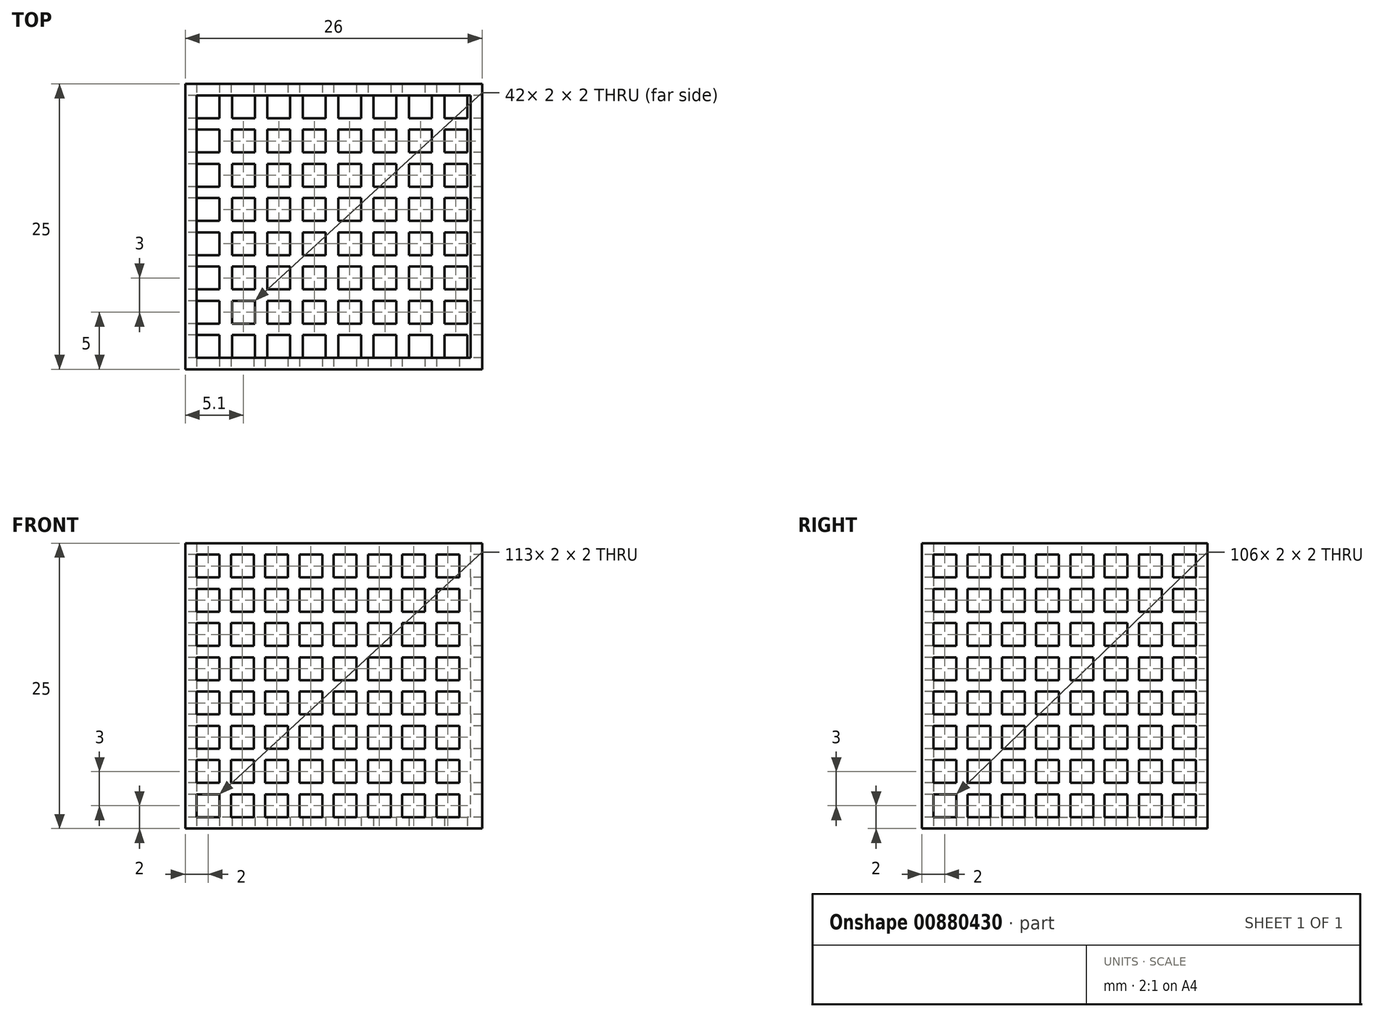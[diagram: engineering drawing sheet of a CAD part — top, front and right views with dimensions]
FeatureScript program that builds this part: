
annotation { "Feature Type Name" : "Feature", "Feature Type Description" : "" }
export const myFeature = defineFeature(function(context is Context, id is Id, definition is map)
    precondition{}
    {
        {
            var Q0;
            Q0=qCreatedBy(makeId("Top.planeOp"),FACE);
            var sketch = newSketch(context, id + "F0", { "sketchPlane" : qUnion([Q0])});
            skLineSegment(sketch, "E0.bottom", {"start": v(13, -12.5) * mm, "end": v(-13, -12.5) * mm});
            skLineSegment(sketch, "E0.top", {"start": v(13, 12.5) * mm, "end": v(-13, 12.5) * mm});
            skLineSegment(sketch, "E0.left", {"start": v(13, -12.5) * mm, "end": v(13, 12.5) * mm});
            skLineSegment(sketch, "E0.right", {"start": v(-13, -12.5) * mm, "end": v(-13, 12.5) * mm});
            skPoint(sketch, "E0.middle", {"position": v(0, 0) * mm});
            skLineSegment(sketch, "E1.bottom", {"start": v(-12, 11.5) * mm, "end": v(-10, 11.5) * mm});
            skLineSegment(sketch, "E1.top", {"start": v(-12, 9.5) * mm, "end": v(-10, 9.5) * mm});
            skLineSegment(sketch, "E1.left", {"start": v(-12, 11.5) * mm, "end": v(-12, 9.5) * mm});
            skLineSegment(sketch, "E1.right", {"start": v(-10, 11.5) * mm, "end": v(-10, 9.5) * mm});
            skLineSegment(sketch, "E2.0.1.0", {"start": v(-12, 8.5) * mm, "end": v(-10, 8.5) * mm});
            skLineSegment(sketch, "E2.0.1.1", {"start": v(-10, 8.5) * mm, "end": v(-10, 6.5) * mm});
            skLineSegment(sketch, "E2.0.1.2", {"start": v(-12, 8.5) * mm, "end": v(-12, 6.5) * mm});
            skLineSegment(sketch, "E2.0.1.3", {"start": v(-12, 6.5) * mm, "end": v(-10, 6.5) * mm});
            skLineSegment(sketch, "E2.0.2.0", {"start": v(-12, 5.5) * mm, "end": v(-10, 5.5) * mm});
            skLineSegment(sketch, "E2.0.2.1", {"start": v(-10, 5.5) * mm, "end": v(-10, 3.5) * mm});
            skLineSegment(sketch, "E2.0.2.2", {"start": v(-12, 5.5) * mm, "end": v(-12, 3.5) * mm});
            skLineSegment(sketch, "E2.0.2.3", {"start": v(-12, 3.5) * mm, "end": v(-10, 3.5) * mm});
            skLineSegment(sketch, "E2.0.3.0", {"start": v(-12, 2.5) * mm, "end": v(-10, 2.5) * mm});
            skLineSegment(sketch, "E2.0.3.1", {"start": v(-10, 2.5) * mm, "end": v(-10, 0.5) * mm});
            skLineSegment(sketch, "E2.0.3.2", {"start": v(-12, 2.5) * mm, "end": v(-12, 0.5) * mm});
            skLineSegment(sketch, "E2.0.3.3", {"start": v(-12, 0.5) * mm, "end": v(-10, 0.5) * mm});
            skLineSegment(sketch, "E2.0.4.0", {"start": v(-12, -0.5) * mm, "end": v(-10, -0.5) * mm});
            skLineSegment(sketch, "E2.0.4.1", {"start": v(-10, -0.5) * mm, "end": v(-10, -2.5) * mm});
            skLineSegment(sketch, "E2.0.4.2", {"start": v(-12, -0.5) * mm, "end": v(-12, -2.5) * mm});
            skLineSegment(sketch, "E2.0.4.3", {"start": v(-12, -2.5) * mm, "end": v(-10, -2.5) * mm});
            skLineSegment(sketch, "E2.0.5.0", {"start": v(-12, -3.5) * mm, "end": v(-10, -3.5) * mm});
            skLineSegment(sketch, "E2.0.5.1", {"start": v(-10, -3.5) * mm, "end": v(-10, -5.5) * mm});
            skLineSegment(sketch, "E2.0.5.2", {"start": v(-12, -3.5) * mm, "end": v(-12, -5.5) * mm});
            skLineSegment(sketch, "E2.0.5.3", {"start": v(-12, -5.5) * mm, "end": v(-10, -5.5) * mm});
            skLineSegment(sketch, "E2.0.6.0", {"start": v(-12, -6.5) * mm, "end": v(-10, -6.5) * mm});
            skLineSegment(sketch, "E2.0.6.1", {"start": v(-10, -6.5) * mm, "end": v(-10, -8.5) * mm});
            skLineSegment(sketch, "E2.0.6.2", {"start": v(-12, -6.5) * mm, "end": v(-12, -8.5) * mm});
            skLineSegment(sketch, "E2.0.6.3", {"start": v(-12, -8.5) * mm, "end": v(-10, -8.5) * mm});
            skLineSegment(sketch, "E2.0.7.0", {"start": v(-12, -9.5) * mm, "end": v(-10, -9.5) * mm});
            skLineSegment(sketch, "E2.0.7.1", {"start": v(-10, -9.5) * mm, "end": v(-10, -11.5) * mm});
            skLineSegment(sketch, "E2.0.7.2", {"start": v(-12, -9.5) * mm, "end": v(-12, -11.5) * mm});
            skLineSegment(sketch, "E2.0.7.3", {"start": v(-12, -11.5) * mm, "end": v(-10, -11.5) * mm});
            skLineSegment(sketch, "E2.1.0.0", {"start": v(-8.9, 11.5) * mm, "end": v(-6.9, 11.5) * mm});
            skLineSegment(sketch, "E2.1.0.1", {"start": v(-6.9, 11.5) * mm, "end": v(-6.9, 9.5) * mm});
            skLineSegment(sketch, "E2.1.0.2", {"start": v(-8.9, 11.5) * mm, "end": v(-8.9, 9.5) * mm});
            skLineSegment(sketch, "E2.1.0.3", {"start": v(-8.9, 9.5) * mm, "end": v(-6.9, 9.5) * mm});
            skLineSegment(sketch, "E2.1.1.0", {"start": v(-8.9, 8.5) * mm, "end": v(-6.9, 8.5) * mm});
            skLineSegment(sketch, "E2.1.1.1", {"start": v(-6.9, 8.5) * mm, "end": v(-6.9, 6.5) * mm});
            skLineSegment(sketch, "E2.1.1.2", {"start": v(-8.9, 8.5) * mm, "end": v(-8.9, 6.5) * mm});
            skLineSegment(sketch, "E2.1.1.3", {"start": v(-8.9, 6.5) * mm, "end": v(-6.9, 6.5) * mm});
            skLineSegment(sketch, "E2.1.2.0", {"start": v(-8.9, 5.5) * mm, "end": v(-6.9, 5.5) * mm});
            skLineSegment(sketch, "E2.1.2.1", {"start": v(-6.9, 5.5) * mm, "end": v(-6.9, 3.5) * mm});
            skLineSegment(sketch, "E2.1.2.2", {"start": v(-8.9, 5.5) * mm, "end": v(-8.9, 3.5) * mm});
            skLineSegment(sketch, "E2.1.2.3", {"start": v(-8.9, 3.5) * mm, "end": v(-6.9, 3.5) * mm});
            skLineSegment(sketch, "E2.1.3.0", {"start": v(-8.9, 2.5) * mm, "end": v(-6.9, 2.5) * mm});
            skLineSegment(sketch, "E2.1.3.1", {"start": v(-6.9, 2.5) * mm, "end": v(-6.9, 0.5) * mm});
            skLineSegment(sketch, "E2.1.3.2", {"start": v(-8.9, 2.5) * mm, "end": v(-8.9, 0.5) * mm});
            skLineSegment(sketch, "E2.1.3.3", {"start": v(-8.9, 0.5) * mm, "end": v(-6.9, 0.5) * mm});
            skLineSegment(sketch, "E2.1.4.0", {"start": v(-8.9, -0.5) * mm, "end": v(-6.9, -0.5) * mm});
            skLineSegment(sketch, "E2.1.4.1", {"start": v(-6.9, -0.5) * mm, "end": v(-6.9, -2.5) * mm});
            skLineSegment(sketch, "E2.1.4.2", {"start": v(-8.9, -0.5) * mm, "end": v(-8.9, -2.5) * mm});
            skLineSegment(sketch, "E2.1.4.3", {"start": v(-8.9, -2.5) * mm, "end": v(-6.9, -2.5) * mm});
            skLineSegment(sketch, "E2.1.5.0", {"start": v(-8.9, -3.5) * mm, "end": v(-6.9, -3.5) * mm});
            skLineSegment(sketch, "E2.1.5.1", {"start": v(-6.9, -3.5) * mm, "end": v(-6.9, -5.5) * mm});
            skLineSegment(sketch, "E2.1.5.2", {"start": v(-8.9, -3.5) * mm, "end": v(-8.9, -5.5) * mm});
            skLineSegment(sketch, "E2.1.5.3", {"start": v(-8.9, -5.5) * mm, "end": v(-6.9, -5.5) * mm});
            skLineSegment(sketch, "E2.1.6.0", {"start": v(-8.9, -6.5) * mm, "end": v(-6.9, -6.5) * mm});
            skLineSegment(sketch, "E2.1.6.1", {"start": v(-6.9, -6.5) * mm, "end": v(-6.9, -8.5) * mm});
            skLineSegment(sketch, "E2.1.6.2", {"start": v(-8.9, -6.5) * mm, "end": v(-8.9, -8.5) * mm});
            skLineSegment(sketch, "E2.1.6.3", {"start": v(-8.9, -8.5) * mm, "end": v(-6.9, -8.5) * mm});
            skLineSegment(sketch, "E2.1.7.0", {"start": v(-8.9, -9.5) * mm, "end": v(-6.9, -9.5) * mm});
            skLineSegment(sketch, "E2.1.7.1", {"start": v(-6.9, -9.5) * mm, "end": v(-6.9, -11.5) * mm});
            skLineSegment(sketch, "E2.1.7.2", {"start": v(-8.9, -9.5) * mm, "end": v(-8.9, -11.5) * mm});
            skLineSegment(sketch, "E2.1.7.3", {"start": v(-8.9, -11.5) * mm, "end": v(-6.9, -11.5) * mm});
            skLineSegment(sketch, "E2.2.0.0", {"start": v(-5.8, 11.5) * mm, "end": v(-3.8, 11.5) * mm});
            skLineSegment(sketch, "E2.2.0.1", {"start": v(-3.8, 11.5) * mm, "end": v(-3.8, 9.5) * mm});
            skLineSegment(sketch, "E2.2.0.2", {"start": v(-5.8, 11.5) * mm, "end": v(-5.8, 9.5) * mm});
            skLineSegment(sketch, "E2.2.0.3", {"start": v(-5.8, 9.5) * mm, "end": v(-3.8, 9.5) * mm});
            skLineSegment(sketch, "E2.2.1.0", {"start": v(-5.8, 8.5) * mm, "end": v(-3.8, 8.5) * mm});
            skLineSegment(sketch, "E2.2.1.1", {"start": v(-3.8, 8.5) * mm, "end": v(-3.8, 6.5) * mm});
            skLineSegment(sketch, "E2.2.1.2", {"start": v(-5.8, 8.5) * mm, "end": v(-5.8, 6.5) * mm});
            skLineSegment(sketch, "E2.2.1.3", {"start": v(-5.8, 6.5) * mm, "end": v(-3.8, 6.5) * mm});
            skLineSegment(sketch, "E2.2.2.0", {"start": v(-5.8, 5.5) * mm, "end": v(-3.8, 5.5) * mm});
            skLineSegment(sketch, "E2.2.2.1", {"start": v(-3.8, 5.5) * mm, "end": v(-3.8, 3.5) * mm});
            skLineSegment(sketch, "E2.2.2.2", {"start": v(-5.8, 5.5) * mm, "end": v(-5.8, 3.5) * mm});
            skLineSegment(sketch, "E2.2.2.3", {"start": v(-5.8, 3.5) * mm, "end": v(-3.8, 3.5) * mm});
            skLineSegment(sketch, "E2.2.3.0", {"start": v(-5.8, 2.5) * mm, "end": v(-3.8, 2.5) * mm});
            skLineSegment(sketch, "E2.2.3.1", {"start": v(-3.8, 2.5) * mm, "end": v(-3.8, 0.5) * mm});
            skLineSegment(sketch, "E2.2.3.2", {"start": v(-5.8, 2.5) * mm, "end": v(-5.8, 0.5) * mm});
            skLineSegment(sketch, "E2.2.3.3", {"start": v(-5.8, 0.5) * mm, "end": v(-3.8, 0.5) * mm});
            skLineSegment(sketch, "E2.2.4.0", {"start": v(-5.8, -0.5) * mm, "end": v(-3.8, -0.5) * mm});
            skLineSegment(sketch, "E2.2.4.1", {"start": v(-3.8, -0.5) * mm, "end": v(-3.8, -2.5) * mm});
            skLineSegment(sketch, "E2.2.4.2", {"start": v(-5.8, -0.5) * mm, "end": v(-5.8, -2.5) * mm});
            skLineSegment(sketch, "E2.2.4.3", {"start": v(-5.8, -2.5) * mm, "end": v(-3.8, -2.5) * mm});
            skLineSegment(sketch, "E2.2.5.0", {"start": v(-5.8, -3.5) * mm, "end": v(-3.8, -3.5) * mm});
            skLineSegment(sketch, "E2.2.5.1", {"start": v(-3.8, -3.5) * mm, "end": v(-3.8, -5.5) * mm});
            skLineSegment(sketch, "E2.2.5.2", {"start": v(-5.8, -3.5) * mm, "end": v(-5.8, -5.5) * mm});
            skLineSegment(sketch, "E2.2.5.3", {"start": v(-5.8, -5.5) * mm, "end": v(-3.8, -5.5) * mm});
            skLineSegment(sketch, "E2.2.6.0", {"start": v(-5.8, -6.5) * mm, "end": v(-3.8, -6.5) * mm});
            skLineSegment(sketch, "E2.2.6.1", {"start": v(-3.8, -6.5) * mm, "end": v(-3.8, -8.5) * mm});
            skLineSegment(sketch, "E2.2.6.2", {"start": v(-5.8, -6.5) * mm, "end": v(-5.8, -8.5) * mm});
            skLineSegment(sketch, "E2.2.6.3", {"start": v(-5.8, -8.5) * mm, "end": v(-3.8, -8.5) * mm});
            skLineSegment(sketch, "E2.2.7.0", {"start": v(-5.8, -9.5) * mm, "end": v(-3.8, -9.5) * mm});
            skLineSegment(sketch, "E2.2.7.1", {"start": v(-3.8, -9.5) * mm, "end": v(-3.8, -11.5) * mm});
            skLineSegment(sketch, "E2.2.7.2", {"start": v(-5.8, -9.5) * mm, "end": v(-5.8, -11.5) * mm});
            skLineSegment(sketch, "E2.2.7.3", {"start": v(-5.8, -11.5) * mm, "end": v(-3.8, -11.5) * mm});
            skLineSegment(sketch, "E2.3.0.0", {"start": v(-2.7, 11.5) * mm, "end": v(-0.7, 11.5) * mm});
            skLineSegment(sketch, "E2.3.0.1", {"start": v(-0.7, 11.5) * mm, "end": v(-0.7, 9.5) * mm});
            skLineSegment(sketch, "E2.3.0.2", {"start": v(-2.7, 11.5) * mm, "end": v(-2.7, 9.5) * mm});
            skLineSegment(sketch, "E2.3.0.3", {"start": v(-2.7, 9.5) * mm, "end": v(-0.7, 9.5) * mm});
            skLineSegment(sketch, "E2.3.1.0", {"start": v(-2.7, 8.5) * mm, "end": v(-0.7, 8.5) * mm});
            skLineSegment(sketch, "E2.3.1.1", {"start": v(-0.7, 8.5) * mm, "end": v(-0.7, 6.5) * mm});
            skLineSegment(sketch, "E2.3.1.2", {"start": v(-2.7, 8.5) * mm, "end": v(-2.7, 6.5) * mm});
            skLineSegment(sketch, "E2.3.1.3", {"start": v(-2.7, 6.5) * mm, "end": v(-0.7, 6.5) * mm});
            skLineSegment(sketch, "E2.3.2.0", {"start": v(-2.7, 5.5) * mm, "end": v(-0.7, 5.5) * mm});
            skLineSegment(sketch, "E2.3.2.1", {"start": v(-0.7, 5.5) * mm, "end": v(-0.7, 3.5) * mm});
            skLineSegment(sketch, "E2.3.2.2", {"start": v(-2.7, 5.5) * mm, "end": v(-2.7, 3.5) * mm});
            skLineSegment(sketch, "E2.3.2.3", {"start": v(-2.7, 3.5) * mm, "end": v(-0.7, 3.5) * mm});
            skLineSegment(sketch, "E2.3.3.0", {"start": v(-2.7, 2.5) * mm, "end": v(-0.7, 2.5) * mm});
            skLineSegment(sketch, "E2.3.3.1", {"start": v(-0.7, 2.5) * mm, "end": v(-0.7, 0.5) * mm});
            skLineSegment(sketch, "E2.3.3.2", {"start": v(-2.7, 2.5) * mm, "end": v(-2.7, 0.5) * mm});
            skLineSegment(sketch, "E2.3.3.3", {"start": v(-2.7, 0.5) * mm, "end": v(-0.7, 0.5) * mm});
            skLineSegment(sketch, "E2.3.4.0", {"start": v(-2.7, -0.5) * mm, "end": v(-0.7, -0.5) * mm});
            skLineSegment(sketch, "E2.3.4.1", {"start": v(-0.7, -0.5) * mm, "end": v(-0.7, -2.5) * mm});
            skLineSegment(sketch, "E2.3.4.2", {"start": v(-2.7, -0.5) * mm, "end": v(-2.7, -2.5) * mm});
            skLineSegment(sketch, "E2.3.4.3", {"start": v(-2.7, -2.5) * mm, "end": v(-0.7, -2.5) * mm});
            skLineSegment(sketch, "E2.3.5.0", {"start": v(-2.7, -3.5) * mm, "end": v(-0.7, -3.5) * mm});
            skLineSegment(sketch, "E2.3.5.1", {"start": v(-0.7, -3.5) * mm, "end": v(-0.7, -5.5) * mm});
            skLineSegment(sketch, "E2.3.5.2", {"start": v(-2.7, -3.5) * mm, "end": v(-2.7, -5.5) * mm});
            skLineSegment(sketch, "E2.3.5.3", {"start": v(-2.7, -5.5) * mm, "end": v(-0.7, -5.5) * mm});
            skLineSegment(sketch, "E2.3.6.0", {"start": v(-2.7, -6.5) * mm, "end": v(-0.7, -6.5) * mm});
            skLineSegment(sketch, "E2.3.6.1", {"start": v(-0.7, -6.5) * mm, "end": v(-0.7, -8.5) * mm});
            skLineSegment(sketch, "E2.3.6.2", {"start": v(-2.7, -6.5) * mm, "end": v(-2.7, -8.5) * mm});
            skLineSegment(sketch, "E2.3.6.3", {"start": v(-2.7, -8.5) * mm, "end": v(-0.7, -8.5) * mm});
            skLineSegment(sketch, "E2.3.7.0", {"start": v(-2.7, -9.5) * mm, "end": v(-0.7, -9.5) * mm});
            skLineSegment(sketch, "E2.3.7.1", {"start": v(-0.7, -9.5) * mm, "end": v(-0.7, -11.5) * mm});
            skLineSegment(sketch, "E2.3.7.2", {"start": v(-2.7, -9.5) * mm, "end": v(-2.7, -11.5) * mm});
            skLineSegment(sketch, "E2.3.7.3", {"start": v(-2.7, -11.5) * mm, "end": v(-0.7, -11.5) * mm});
            skLineSegment(sketch, "E2.4.0.0", {"start": v(0.4, 11.5) * mm, "end": v(2.4, 11.5) * mm});
            skLineSegment(sketch, "E2.4.0.1", {"start": v(2.4, 11.5) * mm, "end": v(2.4, 9.5) * mm});
            skLineSegment(sketch, "E2.4.0.2", {"start": v(0.4, 11.5) * mm, "end": v(0.4, 9.5) * mm});
            skLineSegment(sketch, "E2.4.0.3", {"start": v(0.4, 9.5) * mm, "end": v(2.4, 9.5) * mm});
            skLineSegment(sketch, "E2.4.1.0", {"start": v(0.4, 8.5) * mm, "end": v(2.4, 8.5) * mm});
            skLineSegment(sketch, "E2.4.1.1", {"start": v(2.4, 8.5) * mm, "end": v(2.4, 6.5) * mm});
            skLineSegment(sketch, "E2.4.1.2", {"start": v(0.4, 8.5) * mm, "end": v(0.4, 6.5) * mm});
            skLineSegment(sketch, "E2.4.1.3", {"start": v(0.4, 6.5) * mm, "end": v(2.4, 6.5) * mm});
            skLineSegment(sketch, "E2.4.2.0", {"start": v(0.4, 5.5) * mm, "end": v(2.4, 5.5) * mm});
            skLineSegment(sketch, "E2.4.2.1", {"start": v(2.4, 5.5) * mm, "end": v(2.4, 3.5) * mm});
            skLineSegment(sketch, "E2.4.2.2", {"start": v(0.4, 5.5) * mm, "end": v(0.4, 3.5) * mm});
            skLineSegment(sketch, "E2.4.2.3", {"start": v(0.4, 3.5) * mm, "end": v(2.4, 3.5) * mm});
            skLineSegment(sketch, "E2.4.3.0", {"start": v(0.4, 2.5) * mm, "end": v(2.4, 2.5) * mm});
            skLineSegment(sketch, "E2.4.3.1", {"start": v(2.4, 2.5) * mm, "end": v(2.4, 0.5) * mm});
            skLineSegment(sketch, "E2.4.3.2", {"start": v(0.4, 2.5) * mm, "end": v(0.4, 0.5) * mm});
            skLineSegment(sketch, "E2.4.3.3", {"start": v(0.4, 0.5) * mm, "end": v(2.4, 0.5) * mm});
            skLineSegment(sketch, "E2.4.4.0", {"start": v(0.4, -0.5) * mm, "end": v(2.4, -0.5) * mm});
            skLineSegment(sketch, "E2.4.4.1", {"start": v(2.4, -0.5) * mm, "end": v(2.4, -2.5) * mm});
            skLineSegment(sketch, "E2.4.4.2", {"start": v(0.4, -0.5) * mm, "end": v(0.4, -2.5) * mm});
            skLineSegment(sketch, "E2.4.4.3", {"start": v(0.4, -2.5) * mm, "end": v(2.4, -2.5) * mm});
            skLineSegment(sketch, "E2.4.5.0", {"start": v(0.4, -3.5) * mm, "end": v(2.4, -3.5) * mm});
            skLineSegment(sketch, "E2.4.5.1", {"start": v(2.4, -3.5) * mm, "end": v(2.4, -5.5) * mm});
            skLineSegment(sketch, "E2.4.5.2", {"start": v(0.4, -3.5) * mm, "end": v(0.4, -5.5) * mm});
            skLineSegment(sketch, "E2.4.5.3", {"start": v(0.4, -5.5) * mm, "end": v(2.4, -5.5) * mm});
            skLineSegment(sketch, "E2.4.6.0", {"start": v(0.4, -6.5) * mm, "end": v(2.4, -6.5) * mm});
            skLineSegment(sketch, "E2.4.6.1", {"start": v(2.4, -6.5) * mm, "end": v(2.4, -8.5) * mm});
            skLineSegment(sketch, "E2.4.6.2", {"start": v(0.4, -6.5) * mm, "end": v(0.4, -8.5) * mm});
            skLineSegment(sketch, "E2.4.6.3", {"start": v(0.4, -8.5) * mm, "end": v(2.4, -8.5) * mm});
            skLineSegment(sketch, "E2.4.7.0", {"start": v(0.4, -9.5) * mm, "end": v(2.4, -9.5) * mm});
            skLineSegment(sketch, "E2.4.7.1", {"start": v(2.4, -9.5) * mm, "end": v(2.4, -11.5) * mm});
            skLineSegment(sketch, "E2.4.7.2", {"start": v(0.4, -9.5) * mm, "end": v(0.4, -11.5) * mm});
            skLineSegment(sketch, "E2.4.7.3", {"start": v(0.4, -11.5) * mm, "end": v(2.4, -11.5) * mm});
            skLineSegment(sketch, "E2.5.0.0", {"start": v(3.5, 11.5) * mm, "end": v(5.5, 11.5) * mm});
            skLineSegment(sketch, "E2.5.0.1", {"start": v(5.5, 11.5) * mm, "end": v(5.5, 9.5) * mm});
            skLineSegment(sketch, "E2.5.0.2", {"start": v(3.5, 11.5) * mm, "end": v(3.5, 9.5) * mm});
            skLineSegment(sketch, "E2.5.0.3", {"start": v(3.5, 9.5) * mm, "end": v(5.5, 9.5) * mm});
            skLineSegment(sketch, "E2.5.1.0", {"start": v(3.5, 8.5) * mm, "end": v(5.5, 8.5) * mm});
            skLineSegment(sketch, "E2.5.1.1", {"start": v(5.5, 8.5) * mm, "end": v(5.5, 6.5) * mm});
            skLineSegment(sketch, "E2.5.1.2", {"start": v(3.5, 8.5) * mm, "end": v(3.5, 6.5) * mm});
            skLineSegment(sketch, "E2.5.1.3", {"start": v(3.5, 6.5) * mm, "end": v(5.5, 6.5) * mm});
            skLineSegment(sketch, "E2.5.2.0", {"start": v(3.5, 5.5) * mm, "end": v(5.5, 5.5) * mm});
            skLineSegment(sketch, "E2.5.2.1", {"start": v(5.5, 5.5) * mm, "end": v(5.5, 3.5) * mm});
            skLineSegment(sketch, "E2.5.2.2", {"start": v(3.5, 5.5) * mm, "end": v(3.5, 3.5) * mm});
            skLineSegment(sketch, "E2.5.2.3", {"start": v(3.5, 3.5) * mm, "end": v(5.5, 3.5) * mm});
            skLineSegment(sketch, "E2.5.3.0", {"start": v(3.5, 2.5) * mm, "end": v(5.5, 2.5) * mm});
            skLineSegment(sketch, "E2.5.3.1", {"start": v(5.5, 2.5) * mm, "end": v(5.5, 0.5) * mm});
            skLineSegment(sketch, "E2.5.3.2", {"start": v(3.5, 2.5) * mm, "end": v(3.5, 0.5) * mm});
            skLineSegment(sketch, "E2.5.3.3", {"start": v(3.5, 0.5) * mm, "end": v(5.5, 0.5) * mm});
            skLineSegment(sketch, "E2.5.4.0", {"start": v(3.5, -0.5) * mm, "end": v(5.5, -0.5) * mm});
            skLineSegment(sketch, "E2.5.4.1", {"start": v(5.5, -0.5) * mm, "end": v(5.5, -2.5) * mm});
            skLineSegment(sketch, "E2.5.4.2", {"start": v(3.5, -0.5) * mm, "end": v(3.5, -2.5) * mm});
            skLineSegment(sketch, "E2.5.4.3", {"start": v(3.5, -2.5) * mm, "end": v(5.5, -2.5) * mm});
            skLineSegment(sketch, "E2.5.5.0", {"start": v(3.5, -3.5) * mm, "end": v(5.5, -3.5) * mm});
            skLineSegment(sketch, "E2.5.5.1", {"start": v(5.5, -3.5) * mm, "end": v(5.5, -5.5) * mm});
            skLineSegment(sketch, "E2.5.5.2", {"start": v(3.5, -3.5) * mm, "end": v(3.5, -5.5) * mm});
            skLineSegment(sketch, "E2.5.5.3", {"start": v(3.5, -5.5) * mm, "end": v(5.5, -5.5) * mm});
            skLineSegment(sketch, "E2.5.6.0", {"start": v(3.5, -6.5) * mm, "end": v(5.5, -6.5) * mm});
            skLineSegment(sketch, "E2.5.6.1", {"start": v(5.5, -6.5) * mm, "end": v(5.5, -8.5) * mm});
            skLineSegment(sketch, "E2.5.6.2", {"start": v(3.5, -6.5) * mm, "end": v(3.5, -8.5) * mm});
            skLineSegment(sketch, "E2.5.6.3", {"start": v(3.5, -8.5) * mm, "end": v(5.5, -8.5) * mm});
            skLineSegment(sketch, "E2.5.7.0", {"start": v(3.5, -9.5) * mm, "end": v(5.5, -9.5) * mm});
            skLineSegment(sketch, "E2.5.7.1", {"start": v(5.5, -9.5) * mm, "end": v(5.5, -11.5) * mm});
            skLineSegment(sketch, "E2.5.7.2", {"start": v(3.5, -9.5) * mm, "end": v(3.5, -11.5) * mm});
            skLineSegment(sketch, "E2.5.7.3", {"start": v(3.5, -11.5) * mm, "end": v(5.5, -11.5) * mm});
            skLineSegment(sketch, "E2.6.0.0", {"start": v(6.6, 11.5) * mm, "end": v(8.6, 11.5) * mm});
            skLineSegment(sketch, "E2.6.0.1", {"start": v(8.6, 11.5) * mm, "end": v(8.6, 9.5) * mm});
            skLineSegment(sketch, "E2.6.0.2", {"start": v(6.6, 11.5) * mm, "end": v(6.6, 9.5) * mm});
            skLineSegment(sketch, "E2.6.0.3", {"start": v(6.6, 9.5) * mm, "end": v(8.6, 9.5) * mm});
            skLineSegment(sketch, "E2.6.1.0", {"start": v(6.6, 8.5) * mm, "end": v(8.6, 8.5) * mm});
            skLineSegment(sketch, "E2.6.1.1", {"start": v(8.6, 8.5) * mm, "end": v(8.6, 6.5) * mm});
            skLineSegment(sketch, "E2.6.1.2", {"start": v(6.6, 8.5) * mm, "end": v(6.6, 6.5) * mm});
            skLineSegment(sketch, "E2.6.1.3", {"start": v(6.6, 6.5) * mm, "end": v(8.6, 6.5) * mm});
            skLineSegment(sketch, "E2.6.2.0", {"start": v(6.6, 5.5) * mm, "end": v(8.6, 5.5) * mm});
            skLineSegment(sketch, "E2.6.2.1", {"start": v(8.6, 5.5) * mm, "end": v(8.6, 3.5) * mm});
            skLineSegment(sketch, "E2.6.2.2", {"start": v(6.6, 5.5) * mm, "end": v(6.6, 3.5) * mm});
            skLineSegment(sketch, "E2.6.2.3", {"start": v(6.6, 3.5) * mm, "end": v(8.6, 3.5) * mm});
            skLineSegment(sketch, "E2.6.3.0", {"start": v(6.6, 2.5) * mm, "end": v(8.6, 2.5) * mm});
            skLineSegment(sketch, "E2.6.3.1", {"start": v(8.6, 2.5) * mm, "end": v(8.6, 0.5) * mm});
            skLineSegment(sketch, "E2.6.3.2", {"start": v(6.6, 2.5) * mm, "end": v(6.6, 0.5) * mm});
            skLineSegment(sketch, "E2.6.3.3", {"start": v(6.6, 0.5) * mm, "end": v(8.6, 0.5) * mm});
            skLineSegment(sketch, "E2.6.4.0", {"start": v(6.6, -0.5) * mm, "end": v(8.6, -0.5) * mm});
            skLineSegment(sketch, "E2.6.4.1", {"start": v(8.6, -0.5) * mm, "end": v(8.6, -2.5) * mm});
            skLineSegment(sketch, "E2.6.4.2", {"start": v(6.6, -0.5) * mm, "end": v(6.6, -2.5) * mm});
            skLineSegment(sketch, "E2.6.4.3", {"start": v(6.6, -2.5) * mm, "end": v(8.6, -2.5) * mm});
            skLineSegment(sketch, "E2.6.5.0", {"start": v(6.6, -3.5) * mm, "end": v(8.6, -3.5) * mm});
            skLineSegment(sketch, "E2.6.5.1", {"start": v(8.6, -3.5) * mm, "end": v(8.6, -5.5) * mm});
            skLineSegment(sketch, "E2.6.5.2", {"start": v(6.6, -3.5) * mm, "end": v(6.6, -5.5) * mm});
            skLineSegment(sketch, "E2.6.5.3", {"start": v(6.6, -5.5) * mm, "end": v(8.6, -5.5) * mm});
            skLineSegment(sketch, "E2.6.6.0", {"start": v(6.6, -6.5) * mm, "end": v(8.6, -6.5) * mm});
            skLineSegment(sketch, "E2.6.6.1", {"start": v(8.6, -6.5) * mm, "end": v(8.6, -8.5) * mm});
            skLineSegment(sketch, "E2.6.6.2", {"start": v(6.6, -6.5) * mm, "end": v(6.6, -8.5) * mm});
            skLineSegment(sketch, "E2.6.6.3", {"start": v(6.6, -8.5) * mm, "end": v(8.6, -8.5) * mm});
            skLineSegment(sketch, "E2.6.7.0", {"start": v(6.6, -9.5) * mm, "end": v(8.6, -9.5) * mm});
            skLineSegment(sketch, "E2.6.7.1", {"start": v(8.6, -9.5) * mm, "end": v(8.6, -11.5) * mm});
            skLineSegment(sketch, "E2.6.7.2", {"start": v(6.6, -9.5) * mm, "end": v(6.6, -11.5) * mm});
            skLineSegment(sketch, "E2.6.7.3", {"start": v(6.6, -11.5) * mm, "end": v(8.6, -11.5) * mm});
            skLineSegment(sketch, "E2.7.0.0", {"start": v(9.7, 11.5) * mm, "end": v(11.7, 11.5) * mm});
            skLineSegment(sketch, "E2.7.0.1", {"start": v(11.7, 11.5) * mm, "end": v(11.7, 9.5) * mm});
            skLineSegment(sketch, "E2.7.0.2", {"start": v(9.7, 11.5) * mm, "end": v(9.7, 9.5) * mm});
            skLineSegment(sketch, "E2.7.0.3", {"start": v(9.7, 9.5) * mm, "end": v(11.7, 9.5) * mm});
            skLineSegment(sketch, "E2.7.1.0", {"start": v(9.7, 8.5) * mm, "end": v(11.7, 8.5) * mm});
            skLineSegment(sketch, "E2.7.1.1", {"start": v(11.7, 8.5) * mm, "end": v(11.7, 6.5) * mm});
            skLineSegment(sketch, "E2.7.1.2", {"start": v(9.7, 8.5) * mm, "end": v(9.7, 6.5) * mm});
            skLineSegment(sketch, "E2.7.1.3", {"start": v(9.7, 6.5) * mm, "end": v(11.7, 6.5) * mm});
            skLineSegment(sketch, "E2.7.2.0", {"start": v(9.7, 5.5) * mm, "end": v(11.7, 5.5) * mm});
            skLineSegment(sketch, "E2.7.2.1", {"start": v(11.7, 5.5) * mm, "end": v(11.7, 3.5) * mm});
            skLineSegment(sketch, "E2.7.2.2", {"start": v(9.7, 5.5) * mm, "end": v(9.7, 3.5) * mm});
            skLineSegment(sketch, "E2.7.2.3", {"start": v(9.7, 3.5) * mm, "end": v(11.7, 3.5) * mm});
            skLineSegment(sketch, "E2.7.3.0", {"start": v(9.7, 2.5) * mm, "end": v(11.7, 2.5) * mm});
            skLineSegment(sketch, "E2.7.3.1", {"start": v(11.7, 2.5) * mm, "end": v(11.7, 0.5) * mm});
            skLineSegment(sketch, "E2.7.3.2", {"start": v(9.7, 2.5) * mm, "end": v(9.7, 0.5) * mm});
            skLineSegment(sketch, "E2.7.3.3", {"start": v(9.7, 0.5) * mm, "end": v(11.7, 0.5) * mm});
            skLineSegment(sketch, "E2.7.4.0", {"start": v(9.7, -0.5) * mm, "end": v(11.7, -0.5) * mm});
            skLineSegment(sketch, "E2.7.4.1", {"start": v(11.7, -0.5) * mm, "end": v(11.7, -2.5) * mm});
            skLineSegment(sketch, "E2.7.4.2", {"start": v(9.7, -0.5) * mm, "end": v(9.7, -2.5) * mm});
            skLineSegment(sketch, "E2.7.4.3", {"start": v(9.7, -2.5) * mm, "end": v(11.7, -2.5) * mm});
            skLineSegment(sketch, "E2.7.5.0", {"start": v(9.7, -3.5) * mm, "end": v(11.7, -3.5) * mm});
            skLineSegment(sketch, "E2.7.5.1", {"start": v(11.7, -3.5) * mm, "end": v(11.7, -5.5) * mm});
            skLineSegment(sketch, "E2.7.5.2", {"start": v(9.7, -3.5) * mm, "end": v(9.7, -5.5) * mm});
            skLineSegment(sketch, "E2.7.5.3", {"start": v(9.7, -5.5) * mm, "end": v(11.7, -5.5) * mm});
            skLineSegment(sketch, "E2.7.6.0", {"start": v(9.7, -6.5) * mm, "end": v(11.7, -6.5) * mm});
            skLineSegment(sketch, "E2.7.6.1", {"start": v(11.7, -6.5) * mm, "end": v(11.7, -8.5) * mm});
            skLineSegment(sketch, "E2.7.6.2", {"start": v(9.7, -6.5) * mm, "end": v(9.7, -8.5) * mm});
            skLineSegment(sketch, "E2.7.6.3", {"start": v(9.7, -8.5) * mm, "end": v(11.7, -8.5) * mm});
            skLineSegment(sketch, "E2.7.7.0", {"start": v(9.7, -9.5) * mm, "end": v(11.7, -9.5) * mm});
            skLineSegment(sketch, "E2.7.7.1", {"start": v(11.7, -9.5) * mm, "end": v(11.7, -11.5) * mm});
            skLineSegment(sketch, "E2.7.7.2", {"start": v(9.7, -9.5) * mm, "end": v(9.7, -11.5) * mm});
            skLineSegment(sketch, "E2.7.7.3", {"start": v(9.7, -11.5) * mm, "end": v(11.7, -11.5) * mm});
            skLineSegment(sketch, "E2.direction1", {"start": v(-12, 9.5) * mm, "end": v(-8.9, 9.5) * mm, "construction": true});
            skLineSegment(sketch, "E2.direction2", {"start": v(-12, 9.5) * mm, "end": v(-12, 6.5) * mm, "construction": true});
            skSolve(sketch);
        }
        {
            var Q0;
            Q0=makeQuery(id+"F0.imprint","IMPRINT",FACE,{"disambiguationData":[TD([[makeQuery(id+"F0.imprint","IMPRINT",EDGE,{"derivedFrom":sQuery(id+"F0.wireOp",EDGE,"E0.bottom")}),-1.0]])]});
            extrude(context, id + "F1", {"entities" : qUnion([Q0]), "depth" : 1 * mm, "offsetDistance" : 25 * mm});
        }
        {
            var Q0;
            Q0=makeQuery(id+"F1.opExtrude","CAP_FACE",FACE,{"disambiguationData":[OSD([sQuery(id+"F0.wireOp",EDGE,"E0.bottom"),sQuery(id+"F0.wireOp",EDGE,"E0.top"),sQuery(id+"F0.wireOp",EDGE,"E0.left"),sQuery(id+"F0.wireOp",EDGE,"E0.right"),sQuery(id+"F0.wireOp",EDGE,"E1.bottom"),sQuery(id+"F0.wireOp",EDGE,"E1.top"),sQuery(id+"F0.wireOp",EDGE,"E1.left"),sQuery(id+"F0.wireOp",EDGE,"E1.right"),sQuery(id+"F0.wireOp",EDGE,"E2.0.1.0"),sQuery(id+"F0.wireOp",EDGE,"E2.0.1.1"),sQuery(id+"F0.wireOp",EDGE,"E2.0.1.2"),sQuery(id+"F0.wireOp",EDGE,"E2.0.1.3"),sQuery(id+"F0.wireOp",EDGE,"E2.0.2.0"),sQuery(id+"F0.wireOp",EDGE,"E2.0.2.1"),sQuery(id+"F0.wireOp",EDGE,"E2.0.2.2"),sQuery(id+"F0.wireOp",EDGE,"E2.0.2.3"),sQuery(id+"F0.wireOp",EDGE,"E2.0.3.0"),sQuery(id+"F0.wireOp",EDGE,"E2.0.3.1"),sQuery(id+"F0.wireOp",EDGE,"E2.0.3.2"),sQuery(id+"F0.wireOp",EDGE,"E2.0.3.3"),sQuery(id+"F0.wireOp",EDGE,"E2.0.4.0"),sQuery(id+"F0.wireOp",EDGE,"E2.0.4.1"),sQuery(id+"F0.wireOp",EDGE,"E2.0.4.2"),sQuery(id+"F0.wireOp",EDGE,"E2.0.4.3"),sQuery(id+"F0.wireOp",EDGE,"E2.0.5.0"),sQuery(id+"F0.wireOp",EDGE,"E2.0.5.1"),sQuery(id+"F0.wireOp",EDGE,"E2.0.5.2"),sQuery(id+"F0.wireOp",EDGE,"E2.0.5.3"),sQuery(id+"F0.wireOp",EDGE,"E2.0.6.0"),sQuery(id+"F0.wireOp",EDGE,"E2.0.6.1"),sQuery(id+"F0.wireOp",EDGE,"E2.0.6.2"),sQuery(id+"F0.wireOp",EDGE,"E2.0.6.3"),sQuery(id+"F0.wireOp",EDGE,"E2.0.7.0"),sQuery(id+"F0.wireOp",EDGE,"E2.0.7.1"),sQuery(id+"F0.wireOp",EDGE,"E2.0.7.2"),sQuery(id+"F0.wireOp",EDGE,"E2.0.7.3"),sQuery(id+"F0.wireOp",EDGE,"E2.1.0.0"),sQuery(id+"F0.wireOp",EDGE,"E2.1.0.1"),sQuery(id+"F0.wireOp",EDGE,"E2.1.0.2"),sQuery(id+"F0.wireOp",EDGE,"E2.1.0.3"),sQuery(id+"F0.wireOp",EDGE,"E2.1.1.0"),sQuery(id+"F0.wireOp",EDGE,"E2.1.1.1"),sQuery(id+"F0.wireOp",EDGE,"E2.1.1.2"),sQuery(id+"F0.wireOp",EDGE,"E2.1.1.3"),sQuery(id+"F0.wireOp",EDGE,"E2.1.2.0"),sQuery(id+"F0.wireOp",EDGE,"E2.1.2.1"),sQuery(id+"F0.wireOp",EDGE,"E2.1.2.2"),sQuery(id+"F0.wireOp",EDGE,"E2.1.2.3"),sQuery(id+"F0.wireOp",EDGE,"E2.1.3.0"),sQuery(id+"F0.wireOp",EDGE,"E2.1.3.1"),sQuery(id+"F0.wireOp",EDGE,"E2.1.3.2"),sQuery(id+"F0.wireOp",EDGE,"E2.1.3.3"),sQuery(id+"F0.wireOp",EDGE,"E2.1.4.0"),sQuery(id+"F0.wireOp",EDGE,"E2.1.4.1"),sQuery(id+"F0.wireOp",EDGE,"E2.1.4.2"),sQuery(id+"F0.wireOp",EDGE,"E2.1.4.3"),sQuery(id+"F0.wireOp",EDGE,"E2.1.5.0"),sQuery(id+"F0.wireOp",EDGE,"E2.1.5.1"),sQuery(id+"F0.wireOp",EDGE,"E2.1.5.2"),sQuery(id+"F0.wireOp",EDGE,"E2.1.5.3"),sQuery(id+"F0.wireOp",EDGE,"E2.1.6.0"),sQuery(id+"F0.wireOp",EDGE,"E2.1.6.1"),sQuery(id+"F0.wireOp",EDGE,"E2.1.6.2"),sQuery(id+"F0.wireOp",EDGE,"E2.1.6.3"),sQuery(id+"F0.wireOp",EDGE,"E2.1.7.0"),sQuery(id+"F0.wireOp",EDGE,"E2.1.7.1"),sQuery(id+"F0.wireOp",EDGE,"E2.1.7.2"),sQuery(id+"F0.wireOp",EDGE,"E2.1.7.3"),sQuery(id+"F0.wireOp",EDGE,"E2.2.0.0"),sQuery(id+"F0.wireOp",EDGE,"E2.2.0.1"),sQuery(id+"F0.wireOp",EDGE,"E2.2.0.2"),sQuery(id+"F0.wireOp",EDGE,"E2.2.0.3"),sQuery(id+"F0.wireOp",EDGE,"E2.2.1.0"),sQuery(id+"F0.wireOp",EDGE,"E2.2.1.1"),sQuery(id+"F0.wireOp",EDGE,"E2.2.1.2"),sQuery(id+"F0.wireOp",EDGE,"E2.2.1.3"),sQuery(id+"F0.wireOp",EDGE,"E2.2.2.0"),sQuery(id+"F0.wireOp",EDGE,"E2.2.2.1"),sQuery(id+"F0.wireOp",EDGE,"E2.2.2.2"),sQuery(id+"F0.wireOp",EDGE,"E2.2.2.3"),sQuery(id+"F0.wireOp",EDGE,"E2.2.3.0"),sQuery(id+"F0.wireOp",EDGE,"E2.2.3.1"),sQuery(id+"F0.wireOp",EDGE,"E2.2.3.2"),sQuery(id+"F0.wireOp",EDGE,"E2.2.3.3"),sQuery(id+"F0.wireOp",EDGE,"E2.2.4.0"),sQuery(id+"F0.wireOp",EDGE,"E2.2.4.1"),sQuery(id+"F0.wireOp",EDGE,"E2.2.4.2"),sQuery(id+"F0.wireOp",EDGE,"E2.2.4.3"),sQuery(id+"F0.wireOp",EDGE,"E2.2.5.0"),sQuery(id+"F0.wireOp",EDGE,"E2.2.5.1"),sQuery(id+"F0.wireOp",EDGE,"E2.2.5.2"),sQuery(id+"F0.wireOp",EDGE,"E2.2.5.3"),sQuery(id+"F0.wireOp",EDGE,"E2.2.6.0"),sQuery(id+"F0.wireOp",EDGE,"E2.2.6.1"),sQuery(id+"F0.wireOp",EDGE,"E2.2.6.2"),sQuery(id+"F0.wireOp",EDGE,"E2.2.6.3"),sQuery(id+"F0.wireOp",EDGE,"E2.2.7.0"),sQuery(id+"F0.wireOp",EDGE,"E2.2.7.1"),sQuery(id+"F0.wireOp",EDGE,"E2.2.7.2"),sQuery(id+"F0.wireOp",EDGE,"E2.2.7.3"),sQuery(id+"F0.wireOp",EDGE,"E2.3.0.0"),sQuery(id+"F0.wireOp",EDGE,"E2.3.0.1"),sQuery(id+"F0.wireOp",EDGE,"E2.3.0.2"),sQuery(id+"F0.wireOp",EDGE,"E2.3.0.3"),sQuery(id+"F0.wireOp",EDGE,"E2.3.1.0"),sQuery(id+"F0.wireOp",EDGE,"E2.3.1.1"),sQuery(id+"F0.wireOp",EDGE,"E2.3.1.2"),sQuery(id+"F0.wireOp",EDGE,"E2.3.1.3"),sQuery(id+"F0.wireOp",EDGE,"E2.3.2.0"),sQuery(id+"F0.wireOp",EDGE,"E2.3.2.1"),sQuery(id+"F0.wireOp",EDGE,"E2.3.2.2"),sQuery(id+"F0.wireOp",EDGE,"E2.3.2.3"),sQuery(id+"F0.wireOp",EDGE,"E2.3.3.0"),sQuery(id+"F0.wireOp",EDGE,"E2.3.3.1"),sQuery(id+"F0.wireOp",EDGE,"E2.3.3.2"),sQuery(id+"F0.wireOp",EDGE,"E2.3.3.3"),sQuery(id+"F0.wireOp",EDGE,"E2.3.4.0"),sQuery(id+"F0.wireOp",EDGE,"E2.3.4.1"),sQuery(id+"F0.wireOp",EDGE,"E2.3.4.2"),sQuery(id+"F0.wireOp",EDGE,"E2.3.4.3"),sQuery(id+"F0.wireOp",EDGE,"E2.3.5.0"),sQuery(id+"F0.wireOp",EDGE,"E2.3.5.1"),sQuery(id+"F0.wireOp",EDGE,"E2.3.5.2"),sQuery(id+"F0.wireOp",EDGE,"E2.3.5.3"),sQuery(id+"F0.wireOp",EDGE,"E2.3.6.0"),sQuery(id+"F0.wireOp",EDGE,"E2.3.6.1"),sQuery(id+"F0.wireOp",EDGE,"E2.3.6.2"),sQuery(id+"F0.wireOp",EDGE,"E2.3.6.3"),sQuery(id+"F0.wireOp",EDGE,"E2.3.7.0"),sQuery(id+"F0.wireOp",EDGE,"E2.3.7.1"),sQuery(id+"F0.wireOp",EDGE,"E2.3.7.2"),sQuery(id+"F0.wireOp",EDGE,"E2.3.7.3"),sQuery(id+"F0.wireOp",EDGE,"E2.4.0.0"),sQuery(id+"F0.wireOp",EDGE,"E2.4.0.1"),sQuery(id+"F0.wireOp",EDGE,"E2.4.0.2"),sQuery(id+"F0.wireOp",EDGE,"E2.4.0.3"),sQuery(id+"F0.wireOp",EDGE,"E2.4.1.0"),sQuery(id+"F0.wireOp",EDGE,"E2.4.1.1"),sQuery(id+"F0.wireOp",EDGE,"E2.4.1.2"),sQuery(id+"F0.wireOp",EDGE,"E2.4.1.3"),sQuery(id+"F0.wireOp",EDGE,"E2.4.2.0"),sQuery(id+"F0.wireOp",EDGE,"E2.4.2.1"),sQuery(id+"F0.wireOp",EDGE,"E2.4.2.2"),sQuery(id+"F0.wireOp",EDGE,"E2.4.2.3"),sQuery(id+"F0.wireOp",EDGE,"E2.4.3.0"),sQuery(id+"F0.wireOp",EDGE,"E2.4.3.1"),sQuery(id+"F0.wireOp",EDGE,"E2.4.3.2"),sQuery(id+"F0.wireOp",EDGE,"E2.4.3.3"),sQuery(id+"F0.wireOp",EDGE,"E2.4.4.0"),sQuery(id+"F0.wireOp",EDGE,"E2.4.4.1"),sQuery(id+"F0.wireOp",EDGE,"E2.4.4.2"),sQuery(id+"F0.wireOp",EDGE,"E2.4.4.3"),sQuery(id+"F0.wireOp",EDGE,"E2.4.5.0"),sQuery(id+"F0.wireOp",EDGE,"E2.4.5.1"),sQuery(id+"F0.wireOp",EDGE,"E2.4.5.2"),sQuery(id+"F0.wireOp",EDGE,"E2.4.5.3"),sQuery(id+"F0.wireOp",EDGE,"E2.4.6.0"),sQuery(id+"F0.wireOp",EDGE,"E2.4.6.1"),sQuery(id+"F0.wireOp",EDGE,"E2.4.6.2"),sQuery(id+"F0.wireOp",EDGE,"E2.4.6.3"),sQuery(id+"F0.wireOp",EDGE,"E2.4.7.0"),sQuery(id+"F0.wireOp",EDGE,"E2.4.7.1"),sQuery(id+"F0.wireOp",EDGE,"E2.4.7.2"),sQuery(id+"F0.wireOp",EDGE,"E2.4.7.3"),sQuery(id+"F0.wireOp",EDGE,"E2.5.0.0"),sQuery(id+"F0.wireOp",EDGE,"E2.5.0.1"),sQuery(id+"F0.wireOp",EDGE,"E2.5.0.2"),sQuery(id+"F0.wireOp",EDGE,"E2.5.0.3"),sQuery(id+"F0.wireOp",EDGE,"E2.5.1.0"),sQuery(id+"F0.wireOp",EDGE,"E2.5.1.1"),sQuery(id+"F0.wireOp",EDGE,"E2.5.1.2"),sQuery(id+"F0.wireOp",EDGE,"E2.5.1.3"),sQuery(id+"F0.wireOp",EDGE,"E2.5.2.0"),sQuery(id+"F0.wireOp",EDGE,"E2.5.2.1"),sQuery(id+"F0.wireOp",EDGE,"E2.5.2.2"),sQuery(id+"F0.wireOp",EDGE,"E2.5.2.3"),sQuery(id+"F0.wireOp",EDGE,"E2.5.3.0"),sQuery(id+"F0.wireOp",EDGE,"E2.5.3.1"),sQuery(id+"F0.wireOp",EDGE,"E2.5.3.2"),sQuery(id+"F0.wireOp",EDGE,"E2.5.3.3"),sQuery(id+"F0.wireOp",EDGE,"E2.5.4.0"),sQuery(id+"F0.wireOp",EDGE,"E2.5.4.1"),sQuery(id+"F0.wireOp",EDGE,"E2.5.4.2"),sQuery(id+"F0.wireOp",EDGE,"E2.5.4.3"),sQuery(id+"F0.wireOp",EDGE,"E2.5.5.0"),sQuery(id+"F0.wireOp",EDGE,"E2.5.5.1"),sQuery(id+"F0.wireOp",EDGE,"E2.5.5.2"),sQuery(id+"F0.wireOp",EDGE,"E2.5.5.3"),sQuery(id+"F0.wireOp",EDGE,"E2.5.6.0"),sQuery(id+"F0.wireOp",EDGE,"E2.5.6.1"),sQuery(id+"F0.wireOp",EDGE,"E2.5.6.2"),sQuery(id+"F0.wireOp",EDGE,"E2.5.6.3"),sQuery(id+"F0.wireOp",EDGE,"E2.5.7.0"),sQuery(id+"F0.wireOp",EDGE,"E2.5.7.1"),sQuery(id+"F0.wireOp",EDGE,"E2.5.7.2"),sQuery(id+"F0.wireOp",EDGE,"E2.5.7.3"),sQuery(id+"F0.wireOp",EDGE,"E2.6.0.0"),sQuery(id+"F0.wireOp",EDGE,"E2.6.0.1"),sQuery(id+"F0.wireOp",EDGE,"E2.6.0.2"),sQuery(id+"F0.wireOp",EDGE,"E2.6.0.3"),sQuery(id+"F0.wireOp",EDGE,"E2.6.1.0"),sQuery(id+"F0.wireOp",EDGE,"E2.6.1.1"),sQuery(id+"F0.wireOp",EDGE,"E2.6.1.2"),sQuery(id+"F0.wireOp",EDGE,"E2.6.1.3"),sQuery(id+"F0.wireOp",EDGE,"E2.6.2.0"),sQuery(id+"F0.wireOp",EDGE,"E2.6.2.1"),sQuery(id+"F0.wireOp",EDGE,"E2.6.2.2"),sQuery(id+"F0.wireOp",EDGE,"E2.6.2.3"),sQuery(id+"F0.wireOp",EDGE,"E2.6.3.0"),sQuery(id+"F0.wireOp",EDGE,"E2.6.3.1"),sQuery(id+"F0.wireOp",EDGE,"E2.6.3.2"),sQuery(id+"F0.wireOp",EDGE,"E2.6.3.3"),sQuery(id+"F0.wireOp",EDGE,"E2.6.4.0"),sQuery(id+"F0.wireOp",EDGE,"E2.6.4.1"),sQuery(id+"F0.wireOp",EDGE,"E2.6.4.2"),sQuery(id+"F0.wireOp",EDGE,"E2.6.4.3"),sQuery(id+"F0.wireOp",EDGE,"E2.6.5.0"),sQuery(id+"F0.wireOp",EDGE,"E2.6.5.1"),sQuery(id+"F0.wireOp",EDGE,"E2.6.5.2"),sQuery(id+"F0.wireOp",EDGE,"E2.6.5.3"),sQuery(id+"F0.wireOp",EDGE,"E2.6.6.0"),sQuery(id+"F0.wireOp",EDGE,"E2.6.6.1"),sQuery(id+"F0.wireOp",EDGE,"E2.6.6.2"),sQuery(id+"F0.wireOp",EDGE,"E2.6.6.3"),sQuery(id+"F0.wireOp",EDGE,"E2.6.7.0"),sQuery(id+"F0.wireOp",EDGE,"E2.6.7.1"),sQuery(id+"F0.wireOp",EDGE,"E2.6.7.2"),sQuery(id+"F0.wireOp",EDGE,"E2.6.7.3"),sQuery(id+"F0.wireOp",EDGE,"E2.7.0.0"),sQuery(id+"F0.wireOp",EDGE,"E2.7.0.1"),sQuery(id+"F0.wireOp",EDGE,"E2.7.0.2"),sQuery(id+"F0.wireOp",EDGE,"E2.7.0.3"),sQuery(id+"F0.wireOp",EDGE,"E2.7.1.0"),sQuery(id+"F0.wireOp",EDGE,"E2.7.1.1"),sQuery(id+"F0.wireOp",EDGE,"E2.7.1.2"),sQuery(id+"F0.wireOp",EDGE,"E2.7.1.3"),sQuery(id+"F0.wireOp",EDGE,"E2.7.2.0"),sQuery(id+"F0.wireOp",EDGE,"E2.7.2.1"),sQuery(id+"F0.wireOp",EDGE,"E2.7.2.2"),sQuery(id+"F0.wireOp",EDGE,"E2.7.2.3"),sQuery(id+"F0.wireOp",EDGE,"E2.7.3.0"),sQuery(id+"F0.wireOp",EDGE,"E2.7.3.1"),sQuery(id+"F0.wireOp",EDGE,"E2.7.3.2"),sQuery(id+"F0.wireOp",EDGE,"E2.7.3.3"),sQuery(id+"F0.wireOp",EDGE,"E2.7.4.0"),sQuery(id+"F0.wireOp",EDGE,"E2.7.4.1"),sQuery(id+"F0.wireOp",EDGE,"E2.7.4.2"),sQuery(id+"F0.wireOp",EDGE,"E2.7.4.3"),sQuery(id+"F0.wireOp",EDGE,"E2.7.5.0"),sQuery(id+"F0.wireOp",EDGE,"E2.7.5.1"),sQuery(id+"F0.wireOp",EDGE,"E2.7.5.2"),sQuery(id+"F0.wireOp",EDGE,"E2.7.5.3"),sQuery(id+"F0.wireOp",EDGE,"E2.7.6.0"),sQuery(id+"F0.wireOp",EDGE,"E2.7.6.1"),sQuery(id+"F0.wireOp",EDGE,"E2.7.6.2"),sQuery(id+"F0.wireOp",EDGE,"E2.7.6.3"),sQuery(id+"F0.wireOp",EDGE,"E2.7.7.0"),sQuery(id+"F0.wireOp",EDGE,"E2.7.7.1"),sQuery(id+"F0.wireOp",EDGE,"E2.7.7.2"),sQuery(id+"F0.wireOp",EDGE,"E2.7.7.3")])],"isStart":false});
            var sketch = newSketch(context, id + "F2", { "sketchPlane" : qUnion([Q0])});
            skLineSegment(sketch, "E3.bottom", {"start": v(-13, 12.5) * mm, "end": v(13, 12.5) * mm});
            skLineSegment(sketch, "E3.top", {"start": v(-13, -12.5) * mm, "end": v(13, -12.5) * mm});
            skLineSegment(sketch, "E3.left", {"start": v(-13, 12.5) * mm, "end": v(-13, -12.5) * mm});
            skLineSegment(sketch, "E3.right", {"start": v(13, 12.5) * mm, "end": v(13, -12.5) * mm});
            skLineSegment(sketch, "E4.0", {"start": v(-12, 11.5) * mm, "end": v(-12, -11.5) * mm});
            skLineSegment(sketch, "E4.1", {"start": v(-12, 11.5) * mm, "end": v(12, 11.5) * mm});
            skLineSegment(sketch, "E4.2", {"start": v(12, 11.5) * mm, "end": v(12, -11.5) * mm});
            skLineSegment(sketch, "E4.3", {"start": v(-12, -11.5) * mm, "end": v(12, -11.5) * mm});
            skSolve(sketch);
        }
        {
            var Q0;
            Q0=makeQuery(id+"F2.imprint","IMPRINT",FACE,{"disambiguationData":[TD([[makeQuery(id+"F2.imprint","IMPRINT",EDGE,{"derivedFrom":sQuery(id+"F2.wireOp",EDGE,"E3.bottom")}),1.0]])]});
            extrude(context, id + "F3", {"entities" : qUnion([Q0]), "operationType" : NewBodyOperationType.ADD, "depth" : 24 * mm, "offsetDistance" : 25 * mm});
        }
        {
            var Q0;
            Q0=makeQuery(id+"F3.boolean.opBoolean","MERGE",FACE,{"derivedFrom":[makeQuery(id+"F1.opExtrude","SWEPT_FACE",FACE,{"disambiguationData":[OSD([sQuery(id+"F0.wireOp",EDGE,"E0.right")])]}),makeQuery(id+"F3.opExtrude","SWEPT_FACE",FACE,{"disambiguationData":[OSD([sQuery(id+"F2.wireOp",EDGE,"E3.left")])]})]});
            var sketch = newSketch(context, id + "F4", { "sketchPlane" : qUnion([Q0])});
            skLineSegment(sketch, "E5.bottom", {"start": v(-11.5, 24) * mm, "end": v(-9.5, 24) * mm});
            skLineSegment(sketch, "E5.top", {"start": v(-11.5, 22) * mm, "end": v(-9.5, 22) * mm});
            skLineSegment(sketch, "E5.left", {"start": v(-11.5, 24) * mm, "end": v(-11.5, 22) * mm});
            skLineSegment(sketch, "E5.right", {"start": v(-9.5, 24) * mm, "end": v(-9.5, 22) * mm});
            skLineSegment(sketch, "E6.0.1.0", {"start": v(-11.5, 21) * mm, "end": v(-11.5, 19) * mm});
            skLineSegment(sketch, "E6.0.1.1", {"start": v(-11.5, 21) * mm, "end": v(-9.5, 21) * mm});
            skLineSegment(sketch, "E6.0.1.2", {"start": v(-9.5, 21) * mm, "end": v(-9.5, 19) * mm});
            skLineSegment(sketch, "E6.0.1.3", {"start": v(-11.5, 19) * mm, "end": v(-9.5, 19) * mm});
            skLineSegment(sketch, "E6.0.2.0", {"start": v(-11.5, 18) * mm, "end": v(-11.5, 16) * mm});
            skLineSegment(sketch, "E6.0.2.1", {"start": v(-11.5, 18) * mm, "end": v(-9.5, 18) * mm});
            skLineSegment(sketch, "E6.0.2.2", {"start": v(-9.5, 18) * mm, "end": v(-9.5, 16) * mm});
            skLineSegment(sketch, "E6.0.2.3", {"start": v(-11.5, 16) * mm, "end": v(-9.5, 16) * mm});
            skLineSegment(sketch, "E6.0.3.0", {"start": v(-11.5, 15) * mm, "end": v(-11.5, 13) * mm});
            skLineSegment(sketch, "E6.0.3.1", {"start": v(-11.5, 15) * mm, "end": v(-9.5, 15) * mm});
            skLineSegment(sketch, "E6.0.3.2", {"start": v(-9.5, 15) * mm, "end": v(-9.5, 13) * mm});
            skLineSegment(sketch, "E6.0.3.3", {"start": v(-11.5, 13) * mm, "end": v(-9.5, 13) * mm});
            skLineSegment(sketch, "E6.0.4.0", {"start": v(-11.5, 12) * mm, "end": v(-11.5, 10) * mm});
            skLineSegment(sketch, "E6.0.4.1", {"start": v(-11.5, 12) * mm, "end": v(-9.5, 12) * mm});
            skLineSegment(sketch, "E6.0.4.2", {"start": v(-9.5, 12) * mm, "end": v(-9.5, 10) * mm});
            skLineSegment(sketch, "E6.0.4.3", {"start": v(-11.5, 10) * mm, "end": v(-9.5, 10) * mm});
            skLineSegment(sketch, "E6.0.5.0", {"start": v(-11.5, 9) * mm, "end": v(-11.5, 7) * mm});
            skLineSegment(sketch, "E6.0.5.1", {"start": v(-11.5, 9) * mm, "end": v(-9.5, 9) * mm});
            skLineSegment(sketch, "E6.0.5.2", {"start": v(-9.5, 9) * mm, "end": v(-9.5, 7) * mm});
            skLineSegment(sketch, "E6.0.5.3", {"start": v(-11.5, 7) * mm, "end": v(-9.5, 7) * mm});
            skLineSegment(sketch, "E6.0.6.0", {"start": v(-11.5, 6) * mm, "end": v(-11.5, 4) * mm});
            skLineSegment(sketch, "E6.0.6.1", {"start": v(-11.5, 6) * mm, "end": v(-9.5, 6) * mm});
            skLineSegment(sketch, "E6.0.6.2", {"start": v(-9.5, 6) * mm, "end": v(-9.5, 4) * mm});
            skLineSegment(sketch, "E6.0.6.3", {"start": v(-11.5, 4) * mm, "end": v(-9.5, 4) * mm});
            skLineSegment(sketch, "E6.0.7.0", {"start": v(-11.5, 3) * mm, "end": v(-11.5, 1) * mm});
            skLineSegment(sketch, "E6.0.7.1", {"start": v(-11.5, 3) * mm, "end": v(-9.5, 3) * mm});
            skLineSegment(sketch, "E6.0.7.2", {"start": v(-9.5, 3) * mm, "end": v(-9.5, 1) * mm});
            skLineSegment(sketch, "E6.0.7.3", {"start": v(-11.5, 1) * mm, "end": v(-9.5, 1) * mm});
            skLineSegment(sketch, "E6.1.0.0", {"start": v(-8.5, 24) * mm, "end": v(-8.5, 22) * mm});
            skLineSegment(sketch, "E6.1.0.1", {"start": v(-8.5, 24) * mm, "end": v(-6.5, 24) * mm});
            skLineSegment(sketch, "E6.1.0.2", {"start": v(-6.5, 24) * mm, "end": v(-6.5, 22) * mm});
            skLineSegment(sketch, "E6.1.0.3", {"start": v(-8.5, 22) * mm, "end": v(-6.5, 22) * mm});
            skLineSegment(sketch, "E6.1.1.0", {"start": v(-8.5, 21) * mm, "end": v(-8.5, 19) * mm});
            skLineSegment(sketch, "E6.1.1.1", {"start": v(-8.5, 21) * mm, "end": v(-6.5, 21) * mm});
            skLineSegment(sketch, "E6.1.1.2", {"start": v(-6.5, 21) * mm, "end": v(-6.5, 19) * mm});
            skLineSegment(sketch, "E6.1.1.3", {"start": v(-8.5, 19) * mm, "end": v(-6.5, 19) * mm});
            skLineSegment(sketch, "E6.1.2.0", {"start": v(-8.5, 18) * mm, "end": v(-8.5, 16) * mm});
            skLineSegment(sketch, "E6.1.2.1", {"start": v(-8.5, 18) * mm, "end": v(-6.5, 18) * mm});
            skLineSegment(sketch, "E6.1.2.2", {"start": v(-6.5, 18) * mm, "end": v(-6.5, 16) * mm});
            skLineSegment(sketch, "E6.1.2.3", {"start": v(-8.5, 16) * mm, "end": v(-6.5, 16) * mm});
            skLineSegment(sketch, "E6.1.3.0", {"start": v(-8.5, 15) * mm, "end": v(-8.5, 13) * mm});
            skLineSegment(sketch, "E6.1.3.1", {"start": v(-8.5, 15) * mm, "end": v(-6.5, 15) * mm});
            skLineSegment(sketch, "E6.1.3.2", {"start": v(-6.5, 15) * mm, "end": v(-6.5, 13) * mm});
            skLineSegment(sketch, "E6.1.3.3", {"start": v(-8.5, 13) * mm, "end": v(-6.5, 13) * mm});
            skLineSegment(sketch, "E6.1.4.0", {"start": v(-8.5, 12) * mm, "end": v(-8.5, 10) * mm});
            skLineSegment(sketch, "E6.1.4.1", {"start": v(-8.5, 12) * mm, "end": v(-6.5, 12) * mm});
            skLineSegment(sketch, "E6.1.4.2", {"start": v(-6.5, 12) * mm, "end": v(-6.5, 10) * mm});
            skLineSegment(sketch, "E6.1.4.3", {"start": v(-8.5, 10) * mm, "end": v(-6.5, 10) * mm});
            skLineSegment(sketch, "E6.1.5.0", {"start": v(-8.5, 9) * mm, "end": v(-8.5, 7) * mm});
            skLineSegment(sketch, "E6.1.5.1", {"start": v(-8.5, 9) * mm, "end": v(-6.5, 9) * mm});
            skLineSegment(sketch, "E6.1.5.2", {"start": v(-6.5, 9) * mm, "end": v(-6.5, 7) * mm});
            skLineSegment(sketch, "E6.1.5.3", {"start": v(-8.5, 7) * mm, "end": v(-6.5, 7) * mm});
            skLineSegment(sketch, "E6.1.6.0", {"start": v(-8.5, 6) * mm, "end": v(-8.5, 4) * mm});
            skLineSegment(sketch, "E6.1.6.1", {"start": v(-8.5, 6) * mm, "end": v(-6.5, 6) * mm});
            skLineSegment(sketch, "E6.1.6.2", {"start": v(-6.5, 6) * mm, "end": v(-6.5, 4) * mm});
            skLineSegment(sketch, "E6.1.6.3", {"start": v(-8.5, 4) * mm, "end": v(-6.5, 4) * mm});
            skLineSegment(sketch, "E6.1.7.0", {"start": v(-8.5, 3) * mm, "end": v(-8.5, 1) * mm});
            skLineSegment(sketch, "E6.1.7.1", {"start": v(-8.5, 3) * mm, "end": v(-6.5, 3) * mm});
            skLineSegment(sketch, "E6.1.7.2", {"start": v(-6.5, 3) * mm, "end": v(-6.5, 1) * mm});
            skLineSegment(sketch, "E6.1.7.3", {"start": v(-8.5, 1) * mm, "end": v(-6.5, 1) * mm});
            skLineSegment(sketch, "E6.2.0.0", {"start": v(-5.5, 24) * mm, "end": v(-5.5, 22) * mm});
            skLineSegment(sketch, "E6.2.0.1", {"start": v(-5.5, 24) * mm, "end": v(-3.5, 24) * mm});
            skLineSegment(sketch, "E6.2.0.2", {"start": v(-3.5, 24) * mm, "end": v(-3.5, 22) * mm});
            skLineSegment(sketch, "E6.2.0.3", {"start": v(-5.5, 22) * mm, "end": v(-3.5, 22) * mm});
            skLineSegment(sketch, "E6.2.1.0", {"start": v(-5.5, 21) * mm, "end": v(-5.5, 19) * mm});
            skLineSegment(sketch, "E6.2.1.1", {"start": v(-5.5, 21) * mm, "end": v(-3.5, 21) * mm});
            skLineSegment(sketch, "E6.2.1.2", {"start": v(-3.5, 21) * mm, "end": v(-3.5, 19) * mm});
            skLineSegment(sketch, "E6.2.1.3", {"start": v(-5.5, 19) * mm, "end": v(-3.5, 19) * mm});
            skLineSegment(sketch, "E6.2.2.0", {"start": v(-5.5, 18) * mm, "end": v(-5.5, 16) * mm});
            skLineSegment(sketch, "E6.2.2.1", {"start": v(-5.5, 18) * mm, "end": v(-3.5, 18) * mm});
            skLineSegment(sketch, "E6.2.2.2", {"start": v(-3.5, 18) * mm, "end": v(-3.5, 16) * mm});
            skLineSegment(sketch, "E6.2.2.3", {"start": v(-5.5, 16) * mm, "end": v(-3.5, 16) * mm});
            skLineSegment(sketch, "E6.2.3.0", {"start": v(-5.5, 15) * mm, "end": v(-5.5, 13) * mm});
            skLineSegment(sketch, "E6.2.3.1", {"start": v(-5.5, 15) * mm, "end": v(-3.5, 15) * mm});
            skLineSegment(sketch, "E6.2.3.2", {"start": v(-3.5, 15) * mm, "end": v(-3.5, 13) * mm});
            skLineSegment(sketch, "E6.2.3.3", {"start": v(-5.5, 13) * mm, "end": v(-3.5, 13) * mm});
            skLineSegment(sketch, "E6.2.4.0", {"start": v(-5.5, 12) * mm, "end": v(-5.5, 10) * mm});
            skLineSegment(sketch, "E6.2.4.1", {"start": v(-5.5, 12) * mm, "end": v(-3.5, 12) * mm});
            skLineSegment(sketch, "E6.2.4.2", {"start": v(-3.5, 12) * mm, "end": v(-3.5, 10) * mm});
            skLineSegment(sketch, "E6.2.4.3", {"start": v(-5.5, 10) * mm, "end": v(-3.5, 10) * mm});
            skLineSegment(sketch, "E6.2.5.0", {"start": v(-5.5, 9) * mm, "end": v(-5.5, 7) * mm});
            skLineSegment(sketch, "E6.2.5.1", {"start": v(-5.5, 9) * mm, "end": v(-3.5, 9) * mm});
            skLineSegment(sketch, "E6.2.5.2", {"start": v(-3.5, 9) * mm, "end": v(-3.5, 7) * mm});
            skLineSegment(sketch, "E6.2.5.3", {"start": v(-5.5, 7) * mm, "end": v(-3.5, 7) * mm});
            skLineSegment(sketch, "E6.2.6.0", {"start": v(-5.5, 6) * mm, "end": v(-5.5, 4) * mm});
            skLineSegment(sketch, "E6.2.6.1", {"start": v(-5.5, 6) * mm, "end": v(-3.5, 6) * mm});
            skLineSegment(sketch, "E6.2.6.2", {"start": v(-3.5, 6) * mm, "end": v(-3.5, 4) * mm});
            skLineSegment(sketch, "E6.2.6.3", {"start": v(-5.5, 4) * mm, "end": v(-3.5, 4) * mm});
            skLineSegment(sketch, "E6.2.7.0", {"start": v(-5.5, 3) * mm, "end": v(-5.5, 1) * mm});
            skLineSegment(sketch, "E6.2.7.1", {"start": v(-5.5, 3) * mm, "end": v(-3.5, 3) * mm});
            skLineSegment(sketch, "E6.2.7.2", {"start": v(-3.5, 3) * mm, "end": v(-3.5, 1) * mm});
            skLineSegment(sketch, "E6.2.7.3", {"start": v(-5.5, 1) * mm, "end": v(-3.5, 1) * mm});
            skLineSegment(sketch, "E6.3.0.0", {"start": v(-2.5, 24) * mm, "end": v(-2.5, 22) * mm});
            skLineSegment(sketch, "E6.3.0.1", {"start": v(-2.5, 24) * mm, "end": v(-0.5, 24) * mm});
            skLineSegment(sketch, "E6.3.0.2", {"start": v(-0.5, 24) * mm, "end": v(-0.5, 22) * mm});
            skLineSegment(sketch, "E6.3.0.3", {"start": v(-2.5, 22) * mm, "end": v(-0.5, 22) * mm});
            skLineSegment(sketch, "E6.3.1.0", {"start": v(-2.5, 21) * mm, "end": v(-2.5, 19) * mm});
            skLineSegment(sketch, "E6.3.1.1", {"start": v(-2.5, 21) * mm, "end": v(-0.5, 21) * mm});
            skLineSegment(sketch, "E6.3.1.2", {"start": v(-0.5, 21) * mm, "end": v(-0.5, 19) * mm});
            skLineSegment(sketch, "E6.3.1.3", {"start": v(-2.5, 19) * mm, "end": v(-0.5, 19) * mm});
            skLineSegment(sketch, "E6.3.2.0", {"start": v(-2.5, 18) * mm, "end": v(-2.5, 16) * mm});
            skLineSegment(sketch, "E6.3.2.1", {"start": v(-2.5, 18) * mm, "end": v(-0.5, 18) * mm});
            skLineSegment(sketch, "E6.3.2.2", {"start": v(-0.5, 18) * mm, "end": v(-0.5, 16) * mm});
            skLineSegment(sketch, "E6.3.2.3", {"start": v(-2.5, 16) * mm, "end": v(-0.5, 16) * mm});
            skLineSegment(sketch, "E6.3.3.0", {"start": v(-2.5, 15) * mm, "end": v(-2.5, 13) * mm});
            skLineSegment(sketch, "E6.3.3.1", {"start": v(-2.5, 15) * mm, "end": v(-0.5, 15) * mm});
            skLineSegment(sketch, "E6.3.3.2", {"start": v(-0.5, 15) * mm, "end": v(-0.5, 13) * mm});
            skLineSegment(sketch, "E6.3.3.3", {"start": v(-2.5, 13) * mm, "end": v(-0.5, 13) * mm});
            skLineSegment(sketch, "E6.3.4.0", {"start": v(-2.5, 12) * mm, "end": v(-2.5, 10) * mm});
            skLineSegment(sketch, "E6.3.4.1", {"start": v(-2.5, 12) * mm, "end": v(-0.5, 12) * mm});
            skLineSegment(sketch, "E6.3.4.2", {"start": v(-0.5, 12) * mm, "end": v(-0.5, 10) * mm});
            skLineSegment(sketch, "E6.3.4.3", {"start": v(-2.5, 10) * mm, "end": v(-0.5, 10) * mm});
            skLineSegment(sketch, "E6.3.5.0", {"start": v(-2.5, 9) * mm, "end": v(-2.5, 7) * mm});
            skLineSegment(sketch, "E6.3.5.1", {"start": v(-2.5, 9) * mm, "end": v(-0.5, 9) * mm});
            skLineSegment(sketch, "E6.3.5.2", {"start": v(-0.5, 9) * mm, "end": v(-0.5, 7) * mm});
            skLineSegment(sketch, "E6.3.5.3", {"start": v(-2.5, 7) * mm, "end": v(-0.5, 7) * mm});
            skLineSegment(sketch, "E6.3.6.0", {"start": v(-2.5, 6) * mm, "end": v(-2.5, 4) * mm});
            skLineSegment(sketch, "E6.3.6.1", {"start": v(-2.5, 6) * mm, "end": v(-0.5, 6) * mm});
            skLineSegment(sketch, "E6.3.6.2", {"start": v(-0.5, 6) * mm, "end": v(-0.5, 4) * mm});
            skLineSegment(sketch, "E6.3.6.3", {"start": v(-2.5, 4) * mm, "end": v(-0.5, 4) * mm});
            skLineSegment(sketch, "E6.3.7.0", {"start": v(-2.5, 3) * mm, "end": v(-2.5, 1) * mm});
            skLineSegment(sketch, "E6.3.7.1", {"start": v(-2.5, 3) * mm, "end": v(-0.5, 3) * mm});
            skLineSegment(sketch, "E6.3.7.2", {"start": v(-0.5, 3) * mm, "end": v(-0.5, 1) * mm});
            skLineSegment(sketch, "E6.3.7.3", {"start": v(-2.5, 1) * mm, "end": v(-0.5, 1) * mm});
            skLineSegment(sketch, "E6.4.0.0", {"start": v(0.5, 24) * mm, "end": v(0.5, 22) * mm});
            skLineSegment(sketch, "E6.4.0.1", {"start": v(0.5, 24) * mm, "end": v(2.5, 24) * mm});
            skLineSegment(sketch, "E6.4.0.2", {"start": v(2.5, 24) * mm, "end": v(2.5, 22) * mm});
            skLineSegment(sketch, "E6.4.0.3", {"start": v(0.5, 22) * mm, "end": v(2.5, 22) * mm});
            skLineSegment(sketch, "E6.4.1.0", {"start": v(0.5, 21) * mm, "end": v(0.5, 19) * mm});
            skLineSegment(sketch, "E6.4.1.1", {"start": v(0.5, 21) * mm, "end": v(2.5, 21) * mm});
            skLineSegment(sketch, "E6.4.1.2", {"start": v(2.5, 21) * mm, "end": v(2.5, 19) * mm});
            skLineSegment(sketch, "E6.4.1.3", {"start": v(0.5, 19) * mm, "end": v(2.5, 19) * mm});
            skLineSegment(sketch, "E6.4.2.0", {"start": v(0.5, 18) * mm, "end": v(0.5, 16) * mm});
            skLineSegment(sketch, "E6.4.2.1", {"start": v(0.5, 18) * mm, "end": v(2.5, 18) * mm});
            skLineSegment(sketch, "E6.4.2.2", {"start": v(2.5, 18) * mm, "end": v(2.5, 16) * mm});
            skLineSegment(sketch, "E6.4.2.3", {"start": v(0.5, 16) * mm, "end": v(2.5, 16) * mm});
            skLineSegment(sketch, "E6.4.3.0", {"start": v(0.5, 15) * mm, "end": v(0.5, 13) * mm});
            skLineSegment(sketch, "E6.4.3.1", {"start": v(0.5, 15) * mm, "end": v(2.5, 15) * mm});
            skLineSegment(sketch, "E6.4.3.2", {"start": v(2.5, 15) * mm, "end": v(2.5, 13) * mm});
            skLineSegment(sketch, "E6.4.3.3", {"start": v(0.5, 13) * mm, "end": v(2.5, 13) * mm});
            skLineSegment(sketch, "E6.4.4.0", {"start": v(0.5, 12) * mm, "end": v(0.5, 10) * mm});
            skLineSegment(sketch, "E6.4.4.1", {"start": v(0.5, 12) * mm, "end": v(2.5, 12) * mm});
            skLineSegment(sketch, "E6.4.4.2", {"start": v(2.5, 12) * mm, "end": v(2.5, 10) * mm});
            skLineSegment(sketch, "E6.4.4.3", {"start": v(0.5, 10) * mm, "end": v(2.5, 10) * mm});
            skLineSegment(sketch, "E6.4.5.0", {"start": v(0.5, 9) * mm, "end": v(0.5, 7) * mm});
            skLineSegment(sketch, "E6.4.5.1", {"start": v(0.5, 9) * mm, "end": v(2.5, 9) * mm});
            skLineSegment(sketch, "E6.4.5.2", {"start": v(2.5, 9) * mm, "end": v(2.5, 7) * mm});
            skLineSegment(sketch, "E6.4.5.3", {"start": v(0.5, 7) * mm, "end": v(2.5, 7) * mm});
            skLineSegment(sketch, "E6.4.6.0", {"start": v(0.5, 6) * mm, "end": v(0.5, 4) * mm});
            skLineSegment(sketch, "E6.4.6.1", {"start": v(0.5, 6) * mm, "end": v(2.5, 6) * mm});
            skLineSegment(sketch, "E6.4.6.2", {"start": v(2.5, 6) * mm, "end": v(2.5, 4) * mm});
            skLineSegment(sketch, "E6.4.6.3", {"start": v(0.5, 4) * mm, "end": v(2.5, 4) * mm});
            skLineSegment(sketch, "E6.4.7.0", {"start": v(0.5, 3) * mm, "end": v(0.5, 1) * mm});
            skLineSegment(sketch, "E6.4.7.1", {"start": v(0.5, 3) * mm, "end": v(2.5, 3) * mm});
            skLineSegment(sketch, "E6.4.7.2", {"start": v(2.5, 3) * mm, "end": v(2.5, 1) * mm});
            skLineSegment(sketch, "E6.4.7.3", {"start": v(0.5, 1) * mm, "end": v(2.5, 1) * mm});
            skLineSegment(sketch, "E6.5.0.0", {"start": v(3.5, 24) * mm, "end": v(3.5, 22) * mm});
            skLineSegment(sketch, "E6.5.0.1", {"start": v(3.5, 24) * mm, "end": v(5.5, 24) * mm});
            skLineSegment(sketch, "E6.5.0.2", {"start": v(5.5, 24) * mm, "end": v(5.5, 22) * mm});
            skLineSegment(sketch, "E6.5.0.3", {"start": v(3.5, 22) * mm, "end": v(5.5, 22) * mm});
            skLineSegment(sketch, "E6.5.1.0", {"start": v(3.5, 21) * mm, "end": v(3.5, 19) * mm});
            skLineSegment(sketch, "E6.5.1.1", {"start": v(3.5, 21) * mm, "end": v(5.5, 21) * mm});
            skLineSegment(sketch, "E6.5.1.2", {"start": v(5.5, 21) * mm, "end": v(5.5, 19) * mm});
            skLineSegment(sketch, "E6.5.1.3", {"start": v(3.5, 19) * mm, "end": v(5.5, 19) * mm});
            skLineSegment(sketch, "E6.5.2.0", {"start": v(3.5, 18) * mm, "end": v(3.5, 16) * mm});
            skLineSegment(sketch, "E6.5.2.1", {"start": v(3.5, 18) * mm, "end": v(5.5, 18) * mm});
            skLineSegment(sketch, "E6.5.2.2", {"start": v(5.5, 18) * mm, "end": v(5.5, 16) * mm});
            skLineSegment(sketch, "E6.5.2.3", {"start": v(3.5, 16) * mm, "end": v(5.5, 16) * mm});
            skLineSegment(sketch, "E6.5.3.0", {"start": v(3.5, 15) * mm, "end": v(3.5, 13) * mm});
            skLineSegment(sketch, "E6.5.3.1", {"start": v(3.5, 15) * mm, "end": v(5.5, 15) * mm});
            skLineSegment(sketch, "E6.5.3.2", {"start": v(5.5, 15) * mm, "end": v(5.5, 13) * mm});
            skLineSegment(sketch, "E6.5.3.3", {"start": v(3.5, 13) * mm, "end": v(5.5, 13) * mm});
            skLineSegment(sketch, "E6.5.4.0", {"start": v(3.5, 12) * mm, "end": v(3.5, 10) * mm});
            skLineSegment(sketch, "E6.5.4.1", {"start": v(3.5, 12) * mm, "end": v(5.5, 12) * mm});
            skLineSegment(sketch, "E6.5.4.2", {"start": v(5.5, 12) * mm, "end": v(5.5, 10) * mm});
            skLineSegment(sketch, "E6.5.4.3", {"start": v(3.5, 10) * mm, "end": v(5.5, 10) * mm});
            skLineSegment(sketch, "E6.5.5.0", {"start": v(3.5, 9) * mm, "end": v(3.5, 7) * mm});
            skLineSegment(sketch, "E6.5.5.1", {"start": v(3.5, 9) * mm, "end": v(5.5, 9) * mm});
            skLineSegment(sketch, "E6.5.5.2", {"start": v(5.5, 9) * mm, "end": v(5.5, 7) * mm});
            skLineSegment(sketch, "E6.5.5.3", {"start": v(3.5, 7) * mm, "end": v(5.5, 7) * mm});
            skLineSegment(sketch, "E6.5.6.0", {"start": v(3.5, 6) * mm, "end": v(3.5, 4) * mm});
            skLineSegment(sketch, "E6.5.6.1", {"start": v(3.5, 6) * mm, "end": v(5.5, 6) * mm});
            skLineSegment(sketch, "E6.5.6.2", {"start": v(5.5, 6) * mm, "end": v(5.5, 4) * mm});
            skLineSegment(sketch, "E6.5.6.3", {"start": v(3.5, 4) * mm, "end": v(5.5, 4) * mm});
            skLineSegment(sketch, "E6.5.7.0", {"start": v(3.5, 3) * mm, "end": v(3.5, 1) * mm});
            skLineSegment(sketch, "E6.5.7.1", {"start": v(3.5, 3) * mm, "end": v(5.5, 3) * mm});
            skLineSegment(sketch, "E6.5.7.2", {"start": v(5.5, 3) * mm, "end": v(5.5, 1) * mm});
            skLineSegment(sketch, "E6.5.7.3", {"start": v(3.5, 1) * mm, "end": v(5.5, 1) * mm});
            skLineSegment(sketch, "E6.6.0.0", {"start": v(6.5, 24) * mm, "end": v(6.5, 22) * mm});
            skLineSegment(sketch, "E6.6.0.1", {"start": v(6.5, 24) * mm, "end": v(8.5, 24) * mm});
            skLineSegment(sketch, "E6.6.0.2", {"start": v(8.5, 24) * mm, "end": v(8.5, 22) * mm});
            skLineSegment(sketch, "E6.6.0.3", {"start": v(6.5, 22) * mm, "end": v(8.5, 22) * mm});
            skLineSegment(sketch, "E6.6.1.0", {"start": v(6.5, 21) * mm, "end": v(6.5, 19) * mm});
            skLineSegment(sketch, "E6.6.1.1", {"start": v(6.5, 21) * mm, "end": v(8.5, 21) * mm});
            skLineSegment(sketch, "E6.6.1.2", {"start": v(8.5, 21) * mm, "end": v(8.5, 19) * mm});
            skLineSegment(sketch, "E6.6.1.3", {"start": v(6.5, 19) * mm, "end": v(8.5, 19) * mm});
            skLineSegment(sketch, "E6.6.2.0", {"start": v(6.5, 18) * mm, "end": v(6.5, 16) * mm});
            skLineSegment(sketch, "E6.6.2.1", {"start": v(6.5, 18) * mm, "end": v(8.5, 18) * mm});
            skLineSegment(sketch, "E6.6.2.2", {"start": v(8.5, 18) * mm, "end": v(8.5, 16) * mm});
            skLineSegment(sketch, "E6.6.2.3", {"start": v(6.5, 16) * mm, "end": v(8.5, 16) * mm});
            skLineSegment(sketch, "E6.6.3.0", {"start": v(6.5, 15) * mm, "end": v(6.5, 13) * mm});
            skLineSegment(sketch, "E6.6.3.1", {"start": v(6.5, 15) * mm, "end": v(8.5, 15) * mm});
            skLineSegment(sketch, "E6.6.3.2", {"start": v(8.5, 15) * mm, "end": v(8.5, 13) * mm});
            skLineSegment(sketch, "E6.6.3.3", {"start": v(6.5, 13) * mm, "end": v(8.5, 13) * mm});
            skLineSegment(sketch, "E6.6.4.0", {"start": v(6.5, 12) * mm, "end": v(6.5, 10) * mm});
            skLineSegment(sketch, "E6.6.4.1", {"start": v(6.5, 12) * mm, "end": v(8.5, 12) * mm});
            skLineSegment(sketch, "E6.6.4.2", {"start": v(8.5, 12) * mm, "end": v(8.5, 10) * mm});
            skLineSegment(sketch, "E6.6.4.3", {"start": v(6.5, 10) * mm, "end": v(8.5, 10) * mm});
            skLineSegment(sketch, "E6.6.5.0", {"start": v(6.5, 9) * mm, "end": v(6.5, 7) * mm});
            skLineSegment(sketch, "E6.6.5.1", {"start": v(6.5, 9) * mm, "end": v(8.5, 9) * mm});
            skLineSegment(sketch, "E6.6.5.2", {"start": v(8.5, 9) * mm, "end": v(8.5, 7) * mm});
            skLineSegment(sketch, "E6.6.5.3", {"start": v(6.5, 7) * mm, "end": v(8.5, 7) * mm});
            skLineSegment(sketch, "E6.6.6.0", {"start": v(6.5, 6) * mm, "end": v(6.5, 4) * mm});
            skLineSegment(sketch, "E6.6.6.1", {"start": v(6.5, 6) * mm, "end": v(8.5, 6) * mm});
            skLineSegment(sketch, "E6.6.6.2", {"start": v(8.5, 6) * mm, "end": v(8.5, 4) * mm});
            skLineSegment(sketch, "E6.6.6.3", {"start": v(6.5, 4) * mm, "end": v(8.5, 4) * mm});
            skLineSegment(sketch, "E6.6.7.0", {"start": v(6.5, 3) * mm, "end": v(6.5, 1) * mm});
            skLineSegment(sketch, "E6.6.7.1", {"start": v(6.5, 3) * mm, "end": v(8.5, 3) * mm});
            skLineSegment(sketch, "E6.6.7.2", {"start": v(8.5, 3) * mm, "end": v(8.5, 1) * mm});
            skLineSegment(sketch, "E6.6.7.3", {"start": v(6.5, 1) * mm, "end": v(8.5, 1) * mm});
            skLineSegment(sketch, "E6.7.0.0", {"start": v(9.5, 24) * mm, "end": v(9.5, 22) * mm});
            skLineSegment(sketch, "E6.7.0.1", {"start": v(9.5, 24) * mm, "end": v(11.5, 24) * mm});
            skLineSegment(sketch, "E6.7.0.2", {"start": v(11.5, 24) * mm, "end": v(11.5, 22) * mm});
            skLineSegment(sketch, "E6.7.0.3", {"start": v(9.5, 22) * mm, "end": v(11.5, 22) * mm});
            skLineSegment(sketch, "E6.7.1.0", {"start": v(9.5, 21) * mm, "end": v(9.5, 19) * mm});
            skLineSegment(sketch, "E6.7.1.1", {"start": v(9.5, 21) * mm, "end": v(11.5, 21) * mm});
            skLineSegment(sketch, "E6.7.1.2", {"start": v(11.5, 21) * mm, "end": v(11.5, 19) * mm});
            skLineSegment(sketch, "E6.7.1.3", {"start": v(9.5, 19) * mm, "end": v(11.5, 19) * mm});
            skLineSegment(sketch, "E6.7.2.0", {"start": v(9.5, 18) * mm, "end": v(9.5, 16) * mm});
            skLineSegment(sketch, "E6.7.2.1", {"start": v(9.5, 18) * mm, "end": v(11.5, 18) * mm});
            skLineSegment(sketch, "E6.7.2.2", {"start": v(11.5, 18) * mm, "end": v(11.5, 16) * mm});
            skLineSegment(sketch, "E6.7.2.3", {"start": v(9.5, 16) * mm, "end": v(11.5, 16) * mm});
            skLineSegment(sketch, "E6.7.3.0", {"start": v(9.5, 15) * mm, "end": v(9.5, 13) * mm});
            skLineSegment(sketch, "E6.7.3.1", {"start": v(9.5, 15) * mm, "end": v(11.5, 15) * mm});
            skLineSegment(sketch, "E6.7.3.2", {"start": v(11.5, 15) * mm, "end": v(11.5, 13) * mm});
            skLineSegment(sketch, "E6.7.3.3", {"start": v(9.5, 13) * mm, "end": v(11.5, 13) * mm});
            skLineSegment(sketch, "E6.7.4.0", {"start": v(9.5, 12) * mm, "end": v(9.5, 10) * mm});
            skLineSegment(sketch, "E6.7.4.1", {"start": v(9.5, 12) * mm, "end": v(11.5, 12) * mm});
            skLineSegment(sketch, "E6.7.4.2", {"start": v(11.5, 12) * mm, "end": v(11.5, 10) * mm});
            skLineSegment(sketch, "E6.7.4.3", {"start": v(9.5, 10) * mm, "end": v(11.5, 10) * mm});
            skLineSegment(sketch, "E6.7.5.0", {"start": v(9.5, 9) * mm, "end": v(9.5, 7) * mm});
            skLineSegment(sketch, "E6.7.5.1", {"start": v(9.5, 9) * mm, "end": v(11.5, 9) * mm});
            skLineSegment(sketch, "E6.7.5.2", {"start": v(11.5, 9) * mm, "end": v(11.5, 7) * mm});
            skLineSegment(sketch, "E6.7.5.3", {"start": v(9.5, 7) * mm, "end": v(11.5, 7) * mm});
            skLineSegment(sketch, "E6.7.6.0", {"start": v(9.5, 6) * mm, "end": v(9.5, 4) * mm});
            skLineSegment(sketch, "E6.7.6.1", {"start": v(9.5, 6) * mm, "end": v(11.5, 6) * mm});
            skLineSegment(sketch, "E6.7.6.2", {"start": v(11.5, 6) * mm, "end": v(11.5, 4) * mm});
            skLineSegment(sketch, "E6.7.6.3", {"start": v(9.5, 4) * mm, "end": v(11.5, 4) * mm});
            skLineSegment(sketch, "E6.7.7.0", {"start": v(9.5, 3) * mm, "end": v(9.5, 1) * mm});
            skLineSegment(sketch, "E6.7.7.1", {"start": v(9.5, 3) * mm, "end": v(11.5, 3) * mm});
            skLineSegment(sketch, "E6.7.7.2", {"start": v(11.5, 3) * mm, "end": v(11.5, 1) * mm});
            skLineSegment(sketch, "E6.7.7.3", {"start": v(9.5, 1) * mm, "end": v(11.5, 1) * mm});
            skLineSegment(sketch, "E6.direction1", {"start": v(-11.5, 22) * mm, "end": v(-8.5, 22) * mm, "construction": true});
            skLineSegment(sketch, "E6.direction2", {"start": v(-11.5, 22) * mm, "end": v(-11.5, 19) * mm, "construction": true});
            skSolve(sketch);
        }
        {
            var Q0;
            Q0=makeQuery(id+"F4.imprint","IMPRINT",FACE,{"disambiguationData":[TD([[makeQuery(id+"F4.imprint","IMPRINT",EDGE,{"derivedFrom":sQuery(id+"F4.wireOp",EDGE,"E5.bottom")}),-1.0]])]});
            var Q1;
            Q1=makeQuery(id+"F4.imprint","IMPRINT",FACE,{"disambiguationData":[TD([[makeQuery(id+"F4.imprint","IMPRINT",EDGE,{"derivedFrom":sQuery(id+"F4.wireOp",EDGE,"E6.1.0.0")}),1.0]])]});
            var Q2;
            Q2=makeQuery(id+"F4.imprint","IMPRINT",FACE,{"disambiguationData":[TD([[makeQuery(id+"F4.imprint","IMPRINT",EDGE,{"derivedFrom":sQuery(id+"F4.wireOp",EDGE,"E6.2.0.0")}),1.0]])]});
            var Q3;
            Q3=makeQuery(id+"F4.imprint","IMPRINT",FACE,{"disambiguationData":[TD([[makeQuery(id+"F4.imprint","IMPRINT",EDGE,{"derivedFrom":sQuery(id+"F4.wireOp",EDGE,"E6.3.0.0")}),1.0]])]});
            var Q4;
            Q4=makeQuery(id+"F4.imprint","IMPRINT",FACE,{"disambiguationData":[TD([[makeQuery(id+"F4.imprint","IMPRINT",EDGE,{"derivedFrom":sQuery(id+"F4.wireOp",EDGE,"E6.4.0.0")}),1.0]])]});
            var Q5;
            Q5=makeQuery(id+"F4.imprint","IMPRINT",FACE,{"disambiguationData":[TD([[makeQuery(id+"F4.imprint","IMPRINT",EDGE,{"derivedFrom":sQuery(id+"F4.wireOp",EDGE,"E6.5.0.0")}),1.0]])]});
            var Q6;
            Q6=makeQuery(id+"F4.imprint","IMPRINT",FACE,{"disambiguationData":[TD([[makeQuery(id+"F4.imprint","IMPRINT",EDGE,{"derivedFrom":sQuery(id+"F4.wireOp",EDGE,"E6.6.0.0")}),1.0]])]});
            var Q7;
            Q7=makeQuery(id+"F4.imprint","IMPRINT",FACE,{"disambiguationData":[TD([[makeQuery(id+"F4.imprint","IMPRINT",EDGE,{"derivedFrom":sQuery(id+"F4.wireOp",EDGE,"E6.7.0.0")}),1.0]])]});
            var Q8;
            Q8=makeQuery(id+"F4.imprint","IMPRINT",FACE,{"disambiguationData":[TD([[makeQuery(id+"F4.imprint","IMPRINT",EDGE,{"derivedFrom":sQuery(id+"F4.wireOp",EDGE,"E6.7.1.0")}),1.0]])]});
            var Q9;
            Q9=makeQuery(id+"F4.imprint","IMPRINT",FACE,{"disambiguationData":[TD([[makeQuery(id+"F4.imprint","IMPRINT",EDGE,{"derivedFrom":sQuery(id+"F4.wireOp",EDGE,"E6.6.1.0")}),1.0]])]});
            var Q10;
            Q10=makeQuery(id+"F4.imprint","IMPRINT",FACE,{"disambiguationData":[TD([[makeQuery(id+"F4.imprint","IMPRINT",EDGE,{"derivedFrom":sQuery(id+"F4.wireOp",EDGE,"E6.5.1.0")}),1.0]])]});
            var Q11;
            Q11=makeQuery(id+"F4.imprint","IMPRINT",FACE,{"disambiguationData":[TD([[makeQuery(id+"F4.imprint","IMPRINT",EDGE,{"derivedFrom":sQuery(id+"F4.wireOp",EDGE,"E6.4.1.0")}),1.0]])]});
            var Q12;
            Q12=makeQuery(id+"F4.imprint","IMPRINT",FACE,{"disambiguationData":[TD([[makeQuery(id+"F4.imprint","IMPRINT",EDGE,{"derivedFrom":sQuery(id+"F4.wireOp",EDGE,"E6.3.1.0")}),1.0]])]});
            var Q13;
            Q13=makeQuery(id+"F4.imprint","IMPRINT",FACE,{"disambiguationData":[TD([[makeQuery(id+"F4.imprint","IMPRINT",EDGE,{"derivedFrom":sQuery(id+"F4.wireOp",EDGE,"E6.2.1.0")}),1.0]])]});
            var Q14;
            Q14=makeQuery(id+"F4.imprint","IMPRINT",FACE,{"disambiguationData":[TD([[makeQuery(id+"F4.imprint","IMPRINT",EDGE,{"derivedFrom":sQuery(id+"F4.wireOp",EDGE,"E6.1.1.0")}),1.0]])]});
            var Q15;
            Q15=makeQuery(id+"F4.imprint","IMPRINT",FACE,{"disambiguationData":[TD([[makeQuery(id+"F4.imprint","IMPRINT",EDGE,{"derivedFrom":sQuery(id+"F4.wireOp",EDGE,"E6.0.1.0")}),1.0]])]});
            var Q16;
            Q16=makeQuery(id+"F4.imprint","IMPRINT",FACE,{"disambiguationData":[TD([[makeQuery(id+"F4.imprint","IMPRINT",EDGE,{"derivedFrom":sQuery(id+"F4.wireOp",EDGE,"E6.0.2.0")}),1.0]])]});
            var Q17;
            Q17=makeQuery(id+"F4.imprint","IMPRINT",FACE,{"disambiguationData":[TD([[makeQuery(id+"F4.imprint","IMPRINT",EDGE,{"derivedFrom":sQuery(id+"F4.wireOp",EDGE,"E6.1.2.0")}),1.0]])]});
            var Q18;
            Q18=makeQuery(id+"F4.imprint","IMPRINT",FACE,{"disambiguationData":[TD([[makeQuery(id+"F4.imprint","IMPRINT",EDGE,{"derivedFrom":sQuery(id+"F4.wireOp",EDGE,"E6.2.2.0")}),1.0]])]});
            var Q19;
            Q19=makeQuery(id+"F4.imprint","IMPRINT",FACE,{"disambiguationData":[TD([[makeQuery(id+"F4.imprint","IMPRINT",EDGE,{"derivedFrom":sQuery(id+"F4.wireOp",EDGE,"E6.3.2.0")}),1.0]])]});
            var Q20;
            Q20=makeQuery(id+"F4.imprint","IMPRINT",FACE,{"disambiguationData":[TD([[makeQuery(id+"F4.imprint","IMPRINT",EDGE,{"derivedFrom":sQuery(id+"F4.wireOp",EDGE,"E6.4.2.0")}),1.0]])]});
            var Q21;
            Q21=makeQuery(id+"F4.imprint","IMPRINT",FACE,{"disambiguationData":[TD([[makeQuery(id+"F4.imprint","IMPRINT",EDGE,{"derivedFrom":sQuery(id+"F4.wireOp",EDGE,"E6.5.2.0")}),1.0]])]});
            var Q22;
            Q22=makeQuery(id+"F4.imprint","IMPRINT",FACE,{"disambiguationData":[TD([[makeQuery(id+"F4.imprint","IMPRINT",EDGE,{"derivedFrom":sQuery(id+"F4.wireOp",EDGE,"E6.6.2.0")}),1.0]])]});
            var Q23;
            Q23=makeQuery(id+"F4.imprint","IMPRINT",FACE,{"disambiguationData":[TD([[makeQuery(id+"F4.imprint","IMPRINT",EDGE,{"derivedFrom":sQuery(id+"F4.wireOp",EDGE,"E6.7.2.0")}),1.0]])]});
            var Q24;
            Q24=makeQuery(id+"F4.imprint","IMPRINT",FACE,{"disambiguationData":[TD([[makeQuery(id+"F4.imprint","IMPRINT",EDGE,{"derivedFrom":sQuery(id+"F4.wireOp",EDGE,"E6.0.3.0")}),1.0]])]});
            var Q25;
            Q25=makeQuery(id+"F4.imprint","IMPRINT",FACE,{"disambiguationData":[TD([[makeQuery(id+"F4.imprint","IMPRINT",EDGE,{"derivedFrom":sQuery(id+"F4.wireOp",EDGE,"E6.1.3.0")}),1.0]])]});
            var Q26;
            Q26=makeQuery(id+"F4.imprint","IMPRINT",FACE,{"disambiguationData":[TD([[makeQuery(id+"F4.imprint","IMPRINT",EDGE,{"derivedFrom":sQuery(id+"F4.wireOp",EDGE,"E6.2.3.0")}),1.0]])]});
            var Q27;
            Q27=makeQuery(id+"F4.imprint","IMPRINT",FACE,{"disambiguationData":[TD([[makeQuery(id+"F4.imprint","IMPRINT",EDGE,{"derivedFrom":sQuery(id+"F4.wireOp",EDGE,"E6.3.3.0")}),1.0]])]});
            var Q28;
            Q28=makeQuery(id+"F4.imprint","IMPRINT",FACE,{"disambiguationData":[TD([[makeQuery(id+"F4.imprint","IMPRINT",EDGE,{"derivedFrom":sQuery(id+"F4.wireOp",EDGE,"E6.3.4.0")}),1.0]])]});
            var Q29;
            Q29=makeQuery(id+"F4.imprint","IMPRINT",FACE,{"disambiguationData":[TD([[makeQuery(id+"F4.imprint","IMPRINT",EDGE,{"derivedFrom":sQuery(id+"F4.wireOp",EDGE,"E6.3.5.0")}),1.0]])]});
            var Q30;
            Q30=makeQuery(id+"F4.imprint","IMPRINT",FACE,{"disambiguationData":[TD([[makeQuery(id+"F4.imprint","IMPRINT",EDGE,{"derivedFrom":sQuery(id+"F4.wireOp",EDGE,"E6.2.5.0")}),1.0]])]});
            var Q31;
            Q31=makeQuery(id+"F4.imprint","IMPRINT",FACE,{"disambiguationData":[TD([[makeQuery(id+"F4.imprint","IMPRINT",EDGE,{"derivedFrom":sQuery(id+"F4.wireOp",EDGE,"E6.2.4.0")}),1.0]])]});
            var Q32;
            Q32=makeQuery(id+"F4.imprint","IMPRINT",FACE,{"disambiguationData":[TD([[makeQuery(id+"F4.imprint","IMPRINT",EDGE,{"derivedFrom":sQuery(id+"F4.wireOp",EDGE,"E6.1.4.0")}),1.0]])]});
            var Q33;
            Q33=makeQuery(id+"F4.imprint","IMPRINT",FACE,{"disambiguationData":[TD([[makeQuery(id+"F4.imprint","IMPRINT",EDGE,{"derivedFrom":sQuery(id+"F4.wireOp",EDGE,"E6.1.5.0")}),1.0]])]});
            var Q34;
            Q34=makeQuery(id+"F4.imprint","IMPRINT",FACE,{"disambiguationData":[TD([[makeQuery(id+"F4.imprint","IMPRINT",EDGE,{"derivedFrom":sQuery(id+"F4.wireOp",EDGE,"E6.0.4.0")}),1.0]])]});
            var Q35;
            Q35=makeQuery(id+"F4.imprint","IMPRINT",FACE,{"disambiguationData":[TD([[makeQuery(id+"F4.imprint","IMPRINT",EDGE,{"derivedFrom":sQuery(id+"F4.wireOp",EDGE,"E6.0.5.0")}),1.0]])]});
            var Q36;
            Q36=makeQuery(id+"F4.imprint","IMPRINT",FACE,{"disambiguationData":[TD([[makeQuery(id+"F4.imprint","IMPRINT",EDGE,{"derivedFrom":sQuery(id+"F4.wireOp",EDGE,"E6.0.6.0")}),1.0]])]});
            var Q37;
            Q37=makeQuery(id+"F4.imprint","IMPRINT",FACE,{"disambiguationData":[TD([[makeQuery(id+"F4.imprint","IMPRINT",EDGE,{"derivedFrom":sQuery(id+"F4.wireOp",EDGE,"E6.0.7.0")}),1.0]])]});
            var Q38;
            Q38=makeQuery(id+"F4.imprint","IMPRINT",FACE,{"disambiguationData":[TD([[makeQuery(id+"F4.imprint","IMPRINT",EDGE,{"derivedFrom":sQuery(id+"F4.wireOp",EDGE,"E6.1.7.0")}),1.0]])]});
            var Q39;
            Q39=makeQuery(id+"F4.imprint","IMPRINT",FACE,{"disambiguationData":[TD([[makeQuery(id+"F4.imprint","IMPRINT",EDGE,{"derivedFrom":sQuery(id+"F4.wireOp",EDGE,"E6.2.7.0")}),1.0]])]});
            var Q40;
            Q40=makeQuery(id+"F4.imprint","IMPRINT",FACE,{"disambiguationData":[TD([[makeQuery(id+"F4.imprint","IMPRINT",EDGE,{"derivedFrom":sQuery(id+"F4.wireOp",EDGE,"E6.1.6.0")}),1.0]])]});
            var Q41;
            Q41=makeQuery(id+"F4.imprint","IMPRINT",FACE,{"disambiguationData":[TD([[makeQuery(id+"F4.imprint","IMPRINT",EDGE,{"derivedFrom":sQuery(id+"F4.wireOp",EDGE,"E6.2.6.0")}),1.0]])]});
            var Q42;
            Q42=makeQuery(id+"F4.imprint","IMPRINT",FACE,{"disambiguationData":[TD([[makeQuery(id+"F4.imprint","IMPRINT",EDGE,{"derivedFrom":sQuery(id+"F4.wireOp",EDGE,"E6.3.6.0")}),1.0]])]});
            var Q43;
            Q43=makeQuery(id+"F4.imprint","IMPRINT",FACE,{"disambiguationData":[TD([[makeQuery(id+"F4.imprint","IMPRINT",EDGE,{"derivedFrom":sQuery(id+"F4.wireOp",EDGE,"E6.3.7.0")}),1.0]])]});
            var Q44;
            Q44=makeQuery(id+"F4.imprint","IMPRINT",FACE,{"disambiguationData":[TD([[makeQuery(id+"F4.imprint","IMPRINT",EDGE,{"derivedFrom":sQuery(id+"F4.wireOp",EDGE,"E6.4.7.0")}),1.0]])]});
            var Q45;
            Q45=makeQuery(id+"F4.imprint","IMPRINT",FACE,{"disambiguationData":[TD([[makeQuery(id+"F4.imprint","IMPRINT",EDGE,{"derivedFrom":sQuery(id+"F4.wireOp",EDGE,"E6.4.6.0")}),1.0]])]});
            var Q46;
            Q46=makeQuery(id+"F4.imprint","IMPRINT",FACE,{"disambiguationData":[TD([[makeQuery(id+"F4.imprint","IMPRINT",EDGE,{"derivedFrom":sQuery(id+"F4.wireOp",EDGE,"E6.5.7.0")}),1.0]])]});
            var Q47;
            Q47=makeQuery(id+"F4.imprint","IMPRINT",FACE,{"disambiguationData":[TD([[makeQuery(id+"F4.imprint","IMPRINT",EDGE,{"derivedFrom":sQuery(id+"F4.wireOp",EDGE,"E6.5.6.0")}),1.0]])]});
            var Q48;
            Q48=makeQuery(id+"F4.imprint","IMPRINT",FACE,{"disambiguationData":[TD([[makeQuery(id+"F4.imprint","IMPRINT",EDGE,{"derivedFrom":sQuery(id+"F4.wireOp",EDGE,"E6.5.5.0")}),1.0]])]});
            var Q49;
            Q49=makeQuery(id+"F4.imprint","IMPRINT",FACE,{"disambiguationData":[TD([[makeQuery(id+"F4.imprint","IMPRINT",EDGE,{"derivedFrom":sQuery(id+"F4.wireOp",EDGE,"E6.5.3.0")}),1.0]])]});
            var Q50;
            Q50=makeQuery(id+"F4.imprint","IMPRINT",FACE,{"disambiguationData":[TD([[makeQuery(id+"F4.imprint","IMPRINT",EDGE,{"derivedFrom":sQuery(id+"F4.wireOp",EDGE,"E6.7.5.0")}),1.0]])]});
            var Q51;
            Q51=makeQuery(id+"F4.imprint","IMPRINT",FACE,{"disambiguationData":[TD([[makeQuery(id+"F4.imprint","IMPRINT",EDGE,{"derivedFrom":sQuery(id+"F4.wireOp",EDGE,"E6.7.6.0")}),1.0]])]});
            var Q52;
            Q52=makeQuery(id+"F4.imprint","IMPRINT",FACE,{"disambiguationData":[TD([[makeQuery(id+"F4.imprint","IMPRINT",EDGE,{"derivedFrom":sQuery(id+"F4.wireOp",EDGE,"E6.7.7.0")}),1.0]])]});
            var Q53;
            Q53=makeQuery(id+"F4.imprint","IMPRINT",FACE,{"disambiguationData":[TD([[makeQuery(id+"F4.imprint","IMPRINT",EDGE,{"derivedFrom":sQuery(id+"F4.wireOp",EDGE,"E6.6.7.0")}),1.0]])]});
            var Q54;
            Q54=makeQuery(id+"F4.imprint","IMPRINT",FACE,{"disambiguationData":[TD([[makeQuery(id+"F4.imprint","IMPRINT",EDGE,{"derivedFrom":sQuery(id+"F4.wireOp",EDGE,"E6.6.6.0")}),1.0]])]});
            var Q55;
            Q55=makeQuery(id+"F4.imprint","IMPRINT",FACE,{"disambiguationData":[TD([[makeQuery(id+"F4.imprint","IMPRINT",EDGE,{"derivedFrom":sQuery(id+"F4.wireOp",EDGE,"E6.6.5.0")}),1.0]])]});
            var Q56;
            Q56=makeQuery(id+"F4.imprint","IMPRINT",FACE,{"disambiguationData":[TD([[makeQuery(id+"F4.imprint","IMPRINT",EDGE,{"derivedFrom":sQuery(id+"F4.wireOp",EDGE,"E6.6.4.0")}),1.0]])]});
            var Q57;
            Q57=makeQuery(id+"F4.imprint","IMPRINT",FACE,{"disambiguationData":[TD([[makeQuery(id+"F4.imprint","IMPRINT",EDGE,{"derivedFrom":sQuery(id+"F4.wireOp",EDGE,"E6.6.3.0")}),1.0]])]});
            var Q58;
            Q58=makeQuery(id+"F4.imprint","IMPRINT",FACE,{"disambiguationData":[TD([[makeQuery(id+"F4.imprint","IMPRINT",EDGE,{"derivedFrom":sQuery(id+"F4.wireOp",EDGE,"E6.5.4.0")}),1.0]])]});
            var Q59;
            Q59=makeQuery(id+"F4.imprint","IMPRINT",FACE,{"disambiguationData":[TD([[makeQuery(id+"F4.imprint","IMPRINT",EDGE,{"derivedFrom":sQuery(id+"F4.wireOp",EDGE,"E6.4.3.0")}),1.0]])]});
            var Q60;
            Q60=makeQuery(id+"F4.imprint","IMPRINT",FACE,{"disambiguationData":[TD([[makeQuery(id+"F4.imprint","IMPRINT",EDGE,{"derivedFrom":sQuery(id+"F4.wireOp",EDGE,"E6.4.4.0")}),1.0]])]});
            var Q61;
            Q61=makeQuery(id+"F4.imprint","IMPRINT",FACE,{"disambiguationData":[TD([[makeQuery(id+"F4.imprint","IMPRINT",EDGE,{"derivedFrom":sQuery(id+"F4.wireOp",EDGE,"E6.4.5.0")}),1.0]])]});
            var Q62;
            Q62=makeQuery(id+"F4.imprint","IMPRINT",FACE,{"disambiguationData":[TD([[makeQuery(id+"F4.imprint","IMPRINT",EDGE,{"derivedFrom":sQuery(id+"F4.wireOp",EDGE,"E6.7.3.0")}),1.0]])]});
            var Q63;
            Q63=makeQuery(id+"F4.imprint","IMPRINT",FACE,{"disambiguationData":[TD([[makeQuery(id+"F4.imprint","IMPRINT",EDGE,{"derivedFrom":sQuery(id+"F4.wireOp",EDGE,"E6.7.4.0")}),1.0]])]});
            extrude(context, id + "F5", {"entities" : qUnion([Q0, Q1, Q2, Q3, Q4, Q5, Q6, Q7, Q8, Q9, Q10, Q11, Q12, Q13, Q14, Q15, Q16, Q17, Q18, Q19, Q20, Q21, Q22, Q23, Q24, Q25, Q26, Q27, Q28, Q29, Q30, Q31, Q32, Q33, Q34, Q35, Q36, Q37, Q38, Q39, Q40, Q41, Q42, Q43, Q44, Q45, Q46, Q47, Q48, Q49, Q50, Q51, Q52, Q53, Q54, Q55, Q56, Q57, Q58, Q59, Q60, Q61, Q62, Q63]), "operationType" : NewBodyOperationType.REMOVE, "oppositeDirection" : true, "depth" : 30 * mm, "offsetDistance" : 25 * mm});
        }
        {
            var Q0;
            Q0=makeQuery(id+"F3.boolean.opBoolean","MERGE",FACE,{"derivedFrom":[makeQuery(id+"F1.opExtrude","SWEPT_FACE",FACE,{"disambiguationData":[OSD([sQuery(id+"F0.wireOp",EDGE,"E0.bottom")])]}),makeQuery(id+"F3.opExtrude","SWEPT_FACE",FACE,{"disambiguationData":[OSD([sQuery(id+"F2.wireOp",EDGE,"E3.top")])]})]});
            var sketch = newSketch(context, id + "F6", { "sketchPlane" : qUnion([Q0])});
            skLineSegment(sketch, "E7.bottom", {"start": v(-12, 1) * mm, "end": v(-10, 1) * mm});
            skLineSegment(sketch, "E7.top", {"start": v(-12, 3) * mm, "end": v(-10, 3) * mm});
            skLineSegment(sketch, "E7.left", {"start": v(-12, 1) * mm, "end": v(-12, 3) * mm});
            skLineSegment(sketch, "E7.right", {"start": v(-10, 1) * mm, "end": v(-10, 3) * mm});
            skLineSegment(sketch, "E8.0.1.0", {"start": v(-12, 4) * mm, "end": v(-10, 4) * mm});
            skLineSegment(sketch, "E8.0.1.1", {"start": v(-12, 6) * mm, "end": v(-10, 6) * mm});
            skLineSegment(sketch, "E8.0.1.2", {"start": v(-10, 4) * mm, "end": v(-10, 6) * mm});
            skLineSegment(sketch, "E8.0.1.3", {"start": v(-12, 4) * mm, "end": v(-12, 6) * mm});
            skLineSegment(sketch, "E8.0.2.0", {"start": v(-12, 7) * mm, "end": v(-10, 7) * mm});
            skLineSegment(sketch, "E8.0.2.1", {"start": v(-12, 9) * mm, "end": v(-10, 9) * mm});
            skLineSegment(sketch, "E8.0.2.2", {"start": v(-10, 7) * mm, "end": v(-10, 9) * mm});
            skLineSegment(sketch, "E8.0.2.3", {"start": v(-12, 7) * mm, "end": v(-12, 9) * mm});
            skLineSegment(sketch, "E8.0.3.0", {"start": v(-12, 10) * mm, "end": v(-10, 10) * mm});
            skLineSegment(sketch, "E8.0.3.1", {"start": v(-12, 12) * mm, "end": v(-10, 12) * mm});
            skLineSegment(sketch, "E8.0.3.2", {"start": v(-10, 10) * mm, "end": v(-10, 12) * mm});
            skLineSegment(sketch, "E8.0.3.3", {"start": v(-12, 10) * mm, "end": v(-12, 12) * mm});
            skLineSegment(sketch, "E8.0.4.0", {"start": v(-12, 13) * mm, "end": v(-10, 13) * mm});
            skLineSegment(sketch, "E8.0.4.1", {"start": v(-12, 15) * mm, "end": v(-10, 15) * mm});
            skLineSegment(sketch, "E8.0.4.2", {"start": v(-10, 13) * mm, "end": v(-10, 15) * mm});
            skLineSegment(sketch, "E8.0.4.3", {"start": v(-12, 13) * mm, "end": v(-12, 15) * mm});
            skLineSegment(sketch, "E8.0.5.0", {"start": v(-12, 16) * mm, "end": v(-10, 16) * mm});
            skLineSegment(sketch, "E8.0.5.1", {"start": v(-12, 18) * mm, "end": v(-10, 18) * mm});
            skLineSegment(sketch, "E8.0.5.2", {"start": v(-10, 16) * mm, "end": v(-10, 18) * mm});
            skLineSegment(sketch, "E8.0.5.3", {"start": v(-12, 16) * mm, "end": v(-12, 18) * mm});
            skLineSegment(sketch, "E8.0.6.0", {"start": v(-12, 19) * mm, "end": v(-10, 19) * mm});
            skLineSegment(sketch, "E8.0.6.1", {"start": v(-12, 21) * mm, "end": v(-10, 21) * mm});
            skLineSegment(sketch, "E8.0.6.2", {"start": v(-10, 19) * mm, "end": v(-10, 21) * mm});
            skLineSegment(sketch, "E8.0.6.3", {"start": v(-12, 19) * mm, "end": v(-12, 21) * mm});
            skLineSegment(sketch, "E8.0.7.0", {"start": v(-12, 22) * mm, "end": v(-10, 22) * mm});
            skLineSegment(sketch, "E8.0.7.1", {"start": v(-12, 24) * mm, "end": v(-10, 24) * mm});
            skLineSegment(sketch, "E8.0.7.2", {"start": v(-10, 22) * mm, "end": v(-10, 24) * mm});
            skLineSegment(sketch, "E8.0.7.3", {"start": v(-12, 22) * mm, "end": v(-12, 24) * mm});
            skLineSegment(sketch, "E8.1.0.0", {"start": v(-9, 1) * mm, "end": v(-7, 1) * mm});
            skLineSegment(sketch, "E8.1.0.1", {"start": v(-9, 3) * mm, "end": v(-7, 3) * mm});
            skLineSegment(sketch, "E8.1.0.2", {"start": v(-7, 1) * mm, "end": v(-7, 3) * mm});
            skLineSegment(sketch, "E8.1.0.3", {"start": v(-9, 1) * mm, "end": v(-9, 3) * mm});
            skLineSegment(sketch, "E8.1.1.0", {"start": v(-9, 4) * mm, "end": v(-7, 4) * mm});
            skLineSegment(sketch, "E8.1.1.1", {"start": v(-9, 6) * mm, "end": v(-7, 6) * mm});
            skLineSegment(sketch, "E8.1.1.2", {"start": v(-7, 4) * mm, "end": v(-7, 6) * mm});
            skLineSegment(sketch, "E8.1.1.3", {"start": v(-9, 4) * mm, "end": v(-9, 6) * mm});
            skLineSegment(sketch, "E8.1.2.0", {"start": v(-9, 7) * mm, "end": v(-7, 7) * mm});
            skLineSegment(sketch, "E8.1.2.1", {"start": v(-9, 9) * mm, "end": v(-7, 9) * mm});
            skLineSegment(sketch, "E8.1.2.2", {"start": v(-7, 7) * mm, "end": v(-7, 9) * mm});
            skLineSegment(sketch, "E8.1.2.3", {"start": v(-9, 7) * mm, "end": v(-9, 9) * mm});
            skLineSegment(sketch, "E8.1.3.0", {"start": v(-9, 10) * mm, "end": v(-7, 10) * mm});
            skLineSegment(sketch, "E8.1.3.1", {"start": v(-9, 12) * mm, "end": v(-7, 12) * mm});
            skLineSegment(sketch, "E8.1.3.2", {"start": v(-7, 10) * mm, "end": v(-7, 12) * mm});
            skLineSegment(sketch, "E8.1.3.3", {"start": v(-9, 10) * mm, "end": v(-9, 12) * mm});
            skLineSegment(sketch, "E8.1.4.0", {"start": v(-9, 13) * mm, "end": v(-7, 13) * mm});
            skLineSegment(sketch, "E8.1.4.1", {"start": v(-9, 15) * mm, "end": v(-7, 15) * mm});
            skLineSegment(sketch, "E8.1.4.2", {"start": v(-7, 13) * mm, "end": v(-7, 15) * mm});
            skLineSegment(sketch, "E8.1.4.3", {"start": v(-9, 13) * mm, "end": v(-9, 15) * mm});
            skLineSegment(sketch, "E8.1.5.0", {"start": v(-9, 16) * mm, "end": v(-7, 16) * mm});
            skLineSegment(sketch, "E8.1.5.1", {"start": v(-9, 18) * mm, "end": v(-7, 18) * mm});
            skLineSegment(sketch, "E8.1.5.2", {"start": v(-7, 16) * mm, "end": v(-7, 18) * mm});
            skLineSegment(sketch, "E8.1.5.3", {"start": v(-9, 16) * mm, "end": v(-9, 18) * mm});
            skLineSegment(sketch, "E8.1.6.0", {"start": v(-9, 19) * mm, "end": v(-7, 19) * mm});
            skLineSegment(sketch, "E8.1.6.1", {"start": v(-9, 21) * mm, "end": v(-7, 21) * mm});
            skLineSegment(sketch, "E8.1.6.2", {"start": v(-7, 19) * mm, "end": v(-7, 21) * mm});
            skLineSegment(sketch, "E8.1.6.3", {"start": v(-9, 19) * mm, "end": v(-9, 21) * mm});
            skLineSegment(sketch, "E8.1.7.0", {"start": v(-9, 22) * mm, "end": v(-7, 22) * mm});
            skLineSegment(sketch, "E8.1.7.1", {"start": v(-9, 24) * mm, "end": v(-7, 24) * mm});
            skLineSegment(sketch, "E8.1.7.2", {"start": v(-7, 22) * mm, "end": v(-7, 24) * mm});
            skLineSegment(sketch, "E8.1.7.3", {"start": v(-9, 22) * mm, "end": v(-9, 24) * mm});
            skLineSegment(sketch, "E8.2.0.0", {"start": v(-6, 1) * mm, "end": v(-4, 1) * mm});
            skLineSegment(sketch, "E8.2.0.1", {"start": v(-6, 3) * mm, "end": v(-4, 3) * mm});
            skLineSegment(sketch, "E8.2.0.2", {"start": v(-4, 1) * mm, "end": v(-4, 3) * mm});
            skLineSegment(sketch, "E8.2.0.3", {"start": v(-6, 1) * mm, "end": v(-6, 3) * mm});
            skLineSegment(sketch, "E8.2.1.0", {"start": v(-6, 4) * mm, "end": v(-4, 4) * mm});
            skLineSegment(sketch, "E8.2.1.1", {"start": v(-6, 6) * mm, "end": v(-4, 6) * mm});
            skLineSegment(sketch, "E8.2.1.2", {"start": v(-4, 4) * mm, "end": v(-4, 6) * mm});
            skLineSegment(sketch, "E8.2.1.3", {"start": v(-6, 4) * mm, "end": v(-6, 6) * mm});
            skLineSegment(sketch, "E8.2.2.0", {"start": v(-6, 7) * mm, "end": v(-4, 7) * mm});
            skLineSegment(sketch, "E8.2.2.1", {"start": v(-6, 9) * mm, "end": v(-4, 9) * mm});
            skLineSegment(sketch, "E8.2.2.2", {"start": v(-4, 7) * mm, "end": v(-4, 9) * mm});
            skLineSegment(sketch, "E8.2.2.3", {"start": v(-6, 7) * mm, "end": v(-6, 9) * mm});
            skLineSegment(sketch, "E8.2.3.0", {"start": v(-6, 10) * mm, "end": v(-4, 10) * mm});
            skLineSegment(sketch, "E8.2.3.1", {"start": v(-6, 12) * mm, "end": v(-4, 12) * mm});
            skLineSegment(sketch, "E8.2.3.2", {"start": v(-4, 10) * mm, "end": v(-4, 12) * mm});
            skLineSegment(sketch, "E8.2.3.3", {"start": v(-6, 10) * mm, "end": v(-6, 12) * mm});
            skLineSegment(sketch, "E8.2.4.0", {"start": v(-6, 13) * mm, "end": v(-4, 13) * mm});
            skLineSegment(sketch, "E8.2.4.1", {"start": v(-6, 15) * mm, "end": v(-4, 15) * mm});
            skLineSegment(sketch, "E8.2.4.2", {"start": v(-4, 13) * mm, "end": v(-4, 15) * mm});
            skLineSegment(sketch, "E8.2.4.3", {"start": v(-6, 13) * mm, "end": v(-6, 15) * mm});
            skLineSegment(sketch, "E8.2.5.0", {"start": v(-6, 16) * mm, "end": v(-4, 16) * mm});
            skLineSegment(sketch, "E8.2.5.1", {"start": v(-6, 18) * mm, "end": v(-4, 18) * mm});
            skLineSegment(sketch, "E8.2.5.2", {"start": v(-4, 16) * mm, "end": v(-4, 18) * mm});
            skLineSegment(sketch, "E8.2.5.3", {"start": v(-6, 16) * mm, "end": v(-6, 18) * mm});
            skLineSegment(sketch, "E8.2.6.0", {"start": v(-6, 19) * mm, "end": v(-4, 19) * mm});
            skLineSegment(sketch, "E8.2.6.1", {"start": v(-6, 21) * mm, "end": v(-4, 21) * mm});
            skLineSegment(sketch, "E8.2.6.2", {"start": v(-4, 19) * mm, "end": v(-4, 21) * mm});
            skLineSegment(sketch, "E8.2.6.3", {"start": v(-6, 19) * mm, "end": v(-6, 21) * mm});
            skLineSegment(sketch, "E8.2.7.0", {"start": v(-6, 22) * mm, "end": v(-4, 22) * mm});
            skLineSegment(sketch, "E8.2.7.1", {"start": v(-6, 24) * mm, "end": v(-4, 24) * mm});
            skLineSegment(sketch, "E8.2.7.2", {"start": v(-4, 22) * mm, "end": v(-4, 24) * mm});
            skLineSegment(sketch, "E8.2.7.3", {"start": v(-6, 22) * mm, "end": v(-6, 24) * mm});
            skLineSegment(sketch, "E8.3.0.0", {"start": v(-3, 1) * mm, "end": v(-1, 1) * mm});
            skLineSegment(sketch, "E8.3.0.1", {"start": v(-3, 3) * mm, "end": v(-1, 3) * mm});
            skLineSegment(sketch, "E8.3.0.2", {"start": v(-1, 1) * mm, "end": v(-1, 3) * mm});
            skLineSegment(sketch, "E8.3.0.3", {"start": v(-3, 1) * mm, "end": v(-3, 3) * mm});
            skLineSegment(sketch, "E8.3.1.0", {"start": v(-3, 4) * mm, "end": v(-1, 4) * mm});
            skLineSegment(sketch, "E8.3.1.1", {"start": v(-3, 6) * mm, "end": v(-1, 6) * mm});
            skLineSegment(sketch, "E8.3.1.2", {"start": v(-1, 4) * mm, "end": v(-1, 6) * mm});
            skLineSegment(sketch, "E8.3.1.3", {"start": v(-3, 4) * mm, "end": v(-3, 6) * mm});
            skLineSegment(sketch, "E8.3.2.0", {"start": v(-3, 7) * mm, "end": v(-1, 7) * mm});
            skLineSegment(sketch, "E8.3.2.1", {"start": v(-3, 9) * mm, "end": v(-1, 9) * mm});
            skLineSegment(sketch, "E8.3.2.2", {"start": v(-1, 7) * mm, "end": v(-1, 9) * mm});
            skLineSegment(sketch, "E8.3.2.3", {"start": v(-3, 7) * mm, "end": v(-3, 9) * mm});
            skLineSegment(sketch, "E8.3.3.0", {"start": v(-3, 10) * mm, "end": v(-1, 10) * mm});
            skLineSegment(sketch, "E8.3.3.1", {"start": v(-3, 12) * mm, "end": v(-1, 12) * mm});
            skLineSegment(sketch, "E8.3.3.2", {"start": v(-1, 10) * mm, "end": v(-1, 12) * mm});
            skLineSegment(sketch, "E8.3.3.3", {"start": v(-3, 10) * mm, "end": v(-3, 12) * mm});
            skLineSegment(sketch, "E8.3.4.0", {"start": v(-3, 13) * mm, "end": v(-1, 13) * mm});
            skLineSegment(sketch, "E8.3.4.1", {"start": v(-3, 15) * mm, "end": v(-1, 15) * mm});
            skLineSegment(sketch, "E8.3.4.2", {"start": v(-1, 13) * mm, "end": v(-1, 15) * mm});
            skLineSegment(sketch, "E8.3.4.3", {"start": v(-3, 13) * mm, "end": v(-3, 15) * mm});
            skLineSegment(sketch, "E8.3.5.0", {"start": v(-3, 16) * mm, "end": v(-1, 16) * mm});
            skLineSegment(sketch, "E8.3.5.1", {"start": v(-3, 18) * mm, "end": v(-1, 18) * mm});
            skLineSegment(sketch, "E8.3.5.2", {"start": v(-1, 16) * mm, "end": v(-1, 18) * mm});
            skLineSegment(sketch, "E8.3.5.3", {"start": v(-3, 16) * mm, "end": v(-3, 18) * mm});
            skLineSegment(sketch, "E8.3.6.0", {"start": v(-3, 19) * mm, "end": v(-1, 19) * mm});
            skLineSegment(sketch, "E8.3.6.1", {"start": v(-3, 21) * mm, "end": v(-1, 21) * mm});
            skLineSegment(sketch, "E8.3.6.2", {"start": v(-1, 19) * mm, "end": v(-1, 21) * mm});
            skLineSegment(sketch, "E8.3.6.3", {"start": v(-3, 19) * mm, "end": v(-3, 21) * mm});
            skLineSegment(sketch, "E8.3.7.0", {"start": v(-3, 22) * mm, "end": v(-1, 22) * mm});
            skLineSegment(sketch, "E8.3.7.1", {"start": v(-3, 24) * mm, "end": v(-1, 24) * mm});
            skLineSegment(sketch, "E8.3.7.2", {"start": v(-1, 22) * mm, "end": v(-1, 24) * mm});
            skLineSegment(sketch, "E8.3.7.3", {"start": v(-3, 22) * mm, "end": v(-3, 24) * mm});
            skLineSegment(sketch, "E8.4.0.0", {"start": v(0, 1) * mm, "end": v(2, 1) * mm});
            skLineSegment(sketch, "E8.4.0.1", {"start": v(0, 3) * mm, "end": v(2, 3) * mm});
            skLineSegment(sketch, "E8.4.0.2", {"start": v(2, 1) * mm, "end": v(2, 3) * mm});
            skLineSegment(sketch, "E8.4.0.3", {"start": v(0, 1) * mm, "end": v(0, 3) * mm});
            skLineSegment(sketch, "E8.4.1.0", {"start": v(0, 4) * mm, "end": v(2, 4) * mm});
            skLineSegment(sketch, "E8.4.1.1", {"start": v(0, 6) * mm, "end": v(2, 6) * mm});
            skLineSegment(sketch, "E8.4.1.2", {"start": v(2, 4) * mm, "end": v(2, 6) * mm});
            skLineSegment(sketch, "E8.4.1.3", {"start": v(0, 4) * mm, "end": v(0, 6) * mm});
            skLineSegment(sketch, "E8.4.2.0", {"start": v(0, 7) * mm, "end": v(2, 7) * mm});
            skLineSegment(sketch, "E8.4.2.1", {"start": v(0, 9) * mm, "end": v(2, 9) * mm});
            skLineSegment(sketch, "E8.4.2.2", {"start": v(2, 7) * mm, "end": v(2, 9) * mm});
            skLineSegment(sketch, "E8.4.2.3", {"start": v(0, 7) * mm, "end": v(0, 9) * mm});
            skLineSegment(sketch, "E8.4.3.0", {"start": v(0, 10) * mm, "end": v(2, 10) * mm});
            skLineSegment(sketch, "E8.4.3.1", {"start": v(0, 12) * mm, "end": v(2, 12) * mm});
            skLineSegment(sketch, "E8.4.3.2", {"start": v(2, 10) * mm, "end": v(2, 12) * mm});
            skLineSegment(sketch, "E8.4.3.3", {"start": v(0, 10) * mm, "end": v(0, 12) * mm});
            skLineSegment(sketch, "E8.4.4.0", {"start": v(0, 13) * mm, "end": v(2, 13) * mm});
            skLineSegment(sketch, "E8.4.4.1", {"start": v(0, 15) * mm, "end": v(2, 15) * mm});
            skLineSegment(sketch, "E8.4.4.2", {"start": v(2, 13) * mm, "end": v(2, 15) * mm});
            skLineSegment(sketch, "E8.4.4.3", {"start": v(0, 13) * mm, "end": v(0, 15) * mm});
            skLineSegment(sketch, "E8.4.5.0", {"start": v(0, 16) * mm, "end": v(2, 16) * mm});
            skLineSegment(sketch, "E8.4.5.1", {"start": v(0, 18) * mm, "end": v(2, 18) * mm});
            skLineSegment(sketch, "E8.4.5.2", {"start": v(2, 16) * mm, "end": v(2, 18) * mm});
            skLineSegment(sketch, "E8.4.5.3", {"start": v(0, 16) * mm, "end": v(0, 18) * mm});
            skLineSegment(sketch, "E8.4.6.0", {"start": v(0, 19) * mm, "end": v(2, 19) * mm});
            skLineSegment(sketch, "E8.4.6.1", {"start": v(0, 21) * mm, "end": v(2, 21) * mm});
            skLineSegment(sketch, "E8.4.6.2", {"start": v(2, 19) * mm, "end": v(2, 21) * mm});
            skLineSegment(sketch, "E8.4.6.3", {"start": v(0, 19) * mm, "end": v(0, 21) * mm});
            skLineSegment(sketch, "E8.4.7.0", {"start": v(0, 22) * mm, "end": v(2, 22) * mm});
            skLineSegment(sketch, "E8.4.7.1", {"start": v(0, 24) * mm, "end": v(2, 24) * mm});
            skLineSegment(sketch, "E8.4.7.2", {"start": v(2, 22) * mm, "end": v(2, 24) * mm});
            skLineSegment(sketch, "E8.4.7.3", {"start": v(0, 22) * mm, "end": v(0, 24) * mm});
            skLineSegment(sketch, "E8.5.0.0", {"start": v(3, 1) * mm, "end": v(5, 1) * mm});
            skLineSegment(sketch, "E8.5.0.1", {"start": v(3, 3) * mm, "end": v(5, 3) * mm});
            skLineSegment(sketch, "E8.5.0.2", {"start": v(5, 1) * mm, "end": v(5, 3) * mm});
            skLineSegment(sketch, "E8.5.0.3", {"start": v(3, 1) * mm, "end": v(3, 3) * mm});
            skLineSegment(sketch, "E8.5.1.0", {"start": v(3, 4) * mm, "end": v(5, 4) * mm});
            skLineSegment(sketch, "E8.5.1.1", {"start": v(3, 6) * mm, "end": v(5, 6) * mm});
            skLineSegment(sketch, "E8.5.1.2", {"start": v(5, 4) * mm, "end": v(5, 6) * mm});
            skLineSegment(sketch, "E8.5.1.3", {"start": v(3, 4) * mm, "end": v(3, 6) * mm});
            skLineSegment(sketch, "E8.5.2.0", {"start": v(3, 7) * mm, "end": v(5, 7) * mm});
            skLineSegment(sketch, "E8.5.2.1", {"start": v(3, 9) * mm, "end": v(5, 9) * mm});
            skLineSegment(sketch, "E8.5.2.2", {"start": v(5, 7) * mm, "end": v(5, 9) * mm});
            skLineSegment(sketch, "E8.5.2.3", {"start": v(3, 7) * mm, "end": v(3, 9) * mm});
            skLineSegment(sketch, "E8.5.3.0", {"start": v(3, 10) * mm, "end": v(5, 10) * mm});
            skLineSegment(sketch, "E8.5.3.1", {"start": v(3, 12) * mm, "end": v(5, 12) * mm});
            skLineSegment(sketch, "E8.5.3.2", {"start": v(5, 10) * mm, "end": v(5, 12) * mm});
            skLineSegment(sketch, "E8.5.3.3", {"start": v(3, 10) * mm, "end": v(3, 12) * mm});
            skLineSegment(sketch, "E8.5.4.0", {"start": v(3, 13) * mm, "end": v(5, 13) * mm});
            skLineSegment(sketch, "E8.5.4.1", {"start": v(3, 15) * mm, "end": v(5, 15) * mm});
            skLineSegment(sketch, "E8.5.4.2", {"start": v(5, 13) * mm, "end": v(5, 15) * mm});
            skLineSegment(sketch, "E8.5.4.3", {"start": v(3, 13) * mm, "end": v(3, 15) * mm});
            skLineSegment(sketch, "E8.5.5.0", {"start": v(3, 16) * mm, "end": v(5, 16) * mm});
            skLineSegment(sketch, "E8.5.5.1", {"start": v(3, 18) * mm, "end": v(5, 18) * mm});
            skLineSegment(sketch, "E8.5.5.2", {"start": v(5, 16) * mm, "end": v(5, 18) * mm});
            skLineSegment(sketch, "E8.5.5.3", {"start": v(3, 16) * mm, "end": v(3, 18) * mm});
            skLineSegment(sketch, "E8.5.6.0", {"start": v(3, 19) * mm, "end": v(5, 19) * mm});
            skLineSegment(sketch, "E8.5.6.1", {"start": v(3, 21) * mm, "end": v(5, 21) * mm});
            skLineSegment(sketch, "E8.5.6.2", {"start": v(5, 19) * mm, "end": v(5, 21) * mm});
            skLineSegment(sketch, "E8.5.6.3", {"start": v(3, 19) * mm, "end": v(3, 21) * mm});
            skLineSegment(sketch, "E8.5.7.0", {"start": v(3, 22) * mm, "end": v(5, 22) * mm});
            skLineSegment(sketch, "E8.5.7.1", {"start": v(3, 24) * mm, "end": v(5, 24) * mm});
            skLineSegment(sketch, "E8.5.7.2", {"start": v(5, 22) * mm, "end": v(5, 24) * mm});
            skLineSegment(sketch, "E8.5.7.3", {"start": v(3, 22) * mm, "end": v(3, 24) * mm});
            skLineSegment(sketch, "E8.6.0.0", {"start": v(6, 1) * mm, "end": v(8, 1) * mm});
            skLineSegment(sketch, "E8.6.0.1", {"start": v(6, 3) * mm, "end": v(8, 3) * mm});
            skLineSegment(sketch, "E8.6.0.2", {"start": v(8, 1) * mm, "end": v(8, 3) * mm});
            skLineSegment(sketch, "E8.6.0.3", {"start": v(6, 1) * mm, "end": v(6, 3) * mm});
            skLineSegment(sketch, "E8.6.1.0", {"start": v(6, 4) * mm, "end": v(8, 4) * mm});
            skLineSegment(sketch, "E8.6.1.1", {"start": v(6, 6) * mm, "end": v(8, 6) * mm});
            skLineSegment(sketch, "E8.6.1.2", {"start": v(8, 4) * mm, "end": v(8, 6) * mm});
            skLineSegment(sketch, "E8.6.1.3", {"start": v(6, 4) * mm, "end": v(6, 6) * mm});
            skLineSegment(sketch, "E8.6.2.0", {"start": v(6, 7) * mm, "end": v(8, 7) * mm});
            skLineSegment(sketch, "E8.6.2.1", {"start": v(6, 9) * mm, "end": v(8, 9) * mm});
            skLineSegment(sketch, "E8.6.2.2", {"start": v(8, 7) * mm, "end": v(8, 9) * mm});
            skLineSegment(sketch, "E8.6.2.3", {"start": v(6, 7) * mm, "end": v(6, 9) * mm});
            skLineSegment(sketch, "E8.6.3.0", {"start": v(6, 10) * mm, "end": v(8, 10) * mm});
            skLineSegment(sketch, "E8.6.3.1", {"start": v(6, 12) * mm, "end": v(8, 12) * mm});
            skLineSegment(sketch, "E8.6.3.2", {"start": v(8, 10) * mm, "end": v(8, 12) * mm});
            skLineSegment(sketch, "E8.6.3.3", {"start": v(6, 10) * mm, "end": v(6, 12) * mm});
            skLineSegment(sketch, "E8.6.4.0", {"start": v(6, 13) * mm, "end": v(8, 13) * mm});
            skLineSegment(sketch, "E8.6.4.1", {"start": v(6, 15) * mm, "end": v(8, 15) * mm});
            skLineSegment(sketch, "E8.6.4.2", {"start": v(8, 13) * mm, "end": v(8, 15) * mm});
            skLineSegment(sketch, "E8.6.4.3", {"start": v(6, 13) * mm, "end": v(6, 15) * mm});
            skLineSegment(sketch, "E8.6.5.0", {"start": v(6, 16) * mm, "end": v(8, 16) * mm});
            skLineSegment(sketch, "E8.6.5.1", {"start": v(6, 18) * mm, "end": v(8, 18) * mm});
            skLineSegment(sketch, "E8.6.5.2", {"start": v(8, 16) * mm, "end": v(8, 18) * mm});
            skLineSegment(sketch, "E8.6.5.3", {"start": v(6, 16) * mm, "end": v(6, 18) * mm});
            skLineSegment(sketch, "E8.6.6.0", {"start": v(6, 19) * mm, "end": v(8, 19) * mm});
            skLineSegment(sketch, "E8.6.6.1", {"start": v(6, 21) * mm, "end": v(8, 21) * mm});
            skLineSegment(sketch, "E8.6.6.2", {"start": v(8, 19) * mm, "end": v(8, 21) * mm});
            skLineSegment(sketch, "E8.6.6.3", {"start": v(6, 19) * mm, "end": v(6, 21) * mm});
            skLineSegment(sketch, "E8.6.7.0", {"start": v(6, 22) * mm, "end": v(8, 22) * mm});
            skLineSegment(sketch, "E8.6.7.1", {"start": v(6, 24) * mm, "end": v(8, 24) * mm});
            skLineSegment(sketch, "E8.6.7.2", {"start": v(8, 22) * mm, "end": v(8, 24) * mm});
            skLineSegment(sketch, "E8.6.7.3", {"start": v(6, 22) * mm, "end": v(6, 24) * mm});
            skLineSegment(sketch, "E8.7.0.0", {"start": v(9, 1) * mm, "end": v(11, 1) * mm});
            skLineSegment(sketch, "E8.7.0.1", {"start": v(9, 3) * mm, "end": v(11, 3) * mm});
            skLineSegment(sketch, "E8.7.0.2", {"start": v(11, 1) * mm, "end": v(11, 3) * mm});
            skLineSegment(sketch, "E8.7.0.3", {"start": v(9, 1) * mm, "end": v(9, 3) * mm});
            skLineSegment(sketch, "E8.7.1.0", {"start": v(9, 4) * mm, "end": v(11, 4) * mm});
            skLineSegment(sketch, "E8.7.1.1", {"start": v(9, 6) * mm, "end": v(11, 6) * mm});
            skLineSegment(sketch, "E8.7.1.2", {"start": v(11, 4) * mm, "end": v(11, 6) * mm});
            skLineSegment(sketch, "E8.7.1.3", {"start": v(9, 4) * mm, "end": v(9, 6) * mm});
            skLineSegment(sketch, "E8.7.2.0", {"start": v(9, 7) * mm, "end": v(11, 7) * mm});
            skLineSegment(sketch, "E8.7.2.1", {"start": v(9, 9) * mm, "end": v(11, 9) * mm});
            skLineSegment(sketch, "E8.7.2.2", {"start": v(11, 7) * mm, "end": v(11, 9) * mm});
            skLineSegment(sketch, "E8.7.2.3", {"start": v(9, 7) * mm, "end": v(9, 9) * mm});
            skLineSegment(sketch, "E8.7.3.0", {"start": v(9, 10) * mm, "end": v(11, 10) * mm});
            skLineSegment(sketch, "E8.7.3.1", {"start": v(9, 12) * mm, "end": v(11, 12) * mm});
            skLineSegment(sketch, "E8.7.3.2", {"start": v(11, 10) * mm, "end": v(11, 12) * mm});
            skLineSegment(sketch, "E8.7.3.3", {"start": v(9, 10) * mm, "end": v(9, 12) * mm});
            skLineSegment(sketch, "E8.7.4.0", {"start": v(9, 13) * mm, "end": v(11, 13) * mm});
            skLineSegment(sketch, "E8.7.4.1", {"start": v(9, 15) * mm, "end": v(11, 15) * mm});
            skLineSegment(sketch, "E8.7.4.2", {"start": v(11, 13) * mm, "end": v(11, 15) * mm});
            skLineSegment(sketch, "E8.7.4.3", {"start": v(9, 13) * mm, "end": v(9, 15) * mm});
            skLineSegment(sketch, "E8.7.5.0", {"start": v(9, 16) * mm, "end": v(11, 16) * mm});
            skLineSegment(sketch, "E8.7.5.1", {"start": v(9, 18) * mm, "end": v(11, 18) * mm});
            skLineSegment(sketch, "E8.7.5.2", {"start": v(11, 16) * mm, "end": v(11, 18) * mm});
            skLineSegment(sketch, "E8.7.5.3", {"start": v(9, 16) * mm, "end": v(9, 18) * mm});
            skLineSegment(sketch, "E8.7.6.0", {"start": v(9, 19) * mm, "end": v(11, 19) * mm});
            skLineSegment(sketch, "E8.7.6.1", {"start": v(9, 21) * mm, "end": v(11, 21) * mm});
            skLineSegment(sketch, "E8.7.6.2", {"start": v(11, 19) * mm, "end": v(11, 21) * mm});
            skLineSegment(sketch, "E8.7.6.3", {"start": v(9, 19) * mm, "end": v(9, 21) * mm});
            skLineSegment(sketch, "E8.7.7.0", {"start": v(9, 22) * mm, "end": v(11, 22) * mm});
            skLineSegment(sketch, "E8.7.7.1", {"start": v(9, 24) * mm, "end": v(11, 24) * mm});
            skLineSegment(sketch, "E8.7.7.2", {"start": v(11, 22) * mm, "end": v(11, 24) * mm});
            skLineSegment(sketch, "E8.7.7.3", {"start": v(9, 22) * mm, "end": v(9, 24) * mm});
            skLineSegment(sketch, "E8.direction1", {"start": v(-12, 1) * mm, "end": v(-9, 1) * mm, "construction": true});
            skLineSegment(sketch, "E8.direction2", {"start": v(-12, 1) * mm, "end": v(-12, 4) * mm, "construction": true});
            skSolve(sketch);
        }
        {
            var Q0;
            Q0=makeQuery(id+"F6.imprint","IMPRINT",FACE,{"disambiguationData":[TD([[makeQuery(id+"F6.imprint","IMPRINT",EDGE,{"derivedFrom":sQuery(id+"F6.wireOp",EDGE,"E8.1.0.0")}),1.0]])]});
            var Q1;
            Q1=makeQuery(id+"F6.imprint","IMPRINT",FACE,{"disambiguationData":[TD([[makeQuery(id+"F6.imprint","IMPRINT",EDGE,{"derivedFrom":sQuery(id+"F6.wireOp",EDGE,"E8.1.1.0")}),1.0]])]});
            var Q2;
            Q2=makeQuery(id+"F6.imprint","IMPRINT",FACE,{"disambiguationData":[TD([[makeQuery(id+"F6.imprint","IMPRINT",EDGE,{"derivedFrom":sQuery(id+"F6.wireOp",EDGE,"E8.1.2.0")}),1.0]])]});
            var Q3;
            Q3=makeQuery(id+"F6.imprint","IMPRINT",FACE,{"disambiguationData":[TD([[makeQuery(id+"F6.imprint","IMPRINT",EDGE,{"derivedFrom":sQuery(id+"F6.wireOp",EDGE,"E8.1.3.0")}),1.0]])]});
            var Q4;
            Q4=makeQuery(id+"F6.imprint","IMPRINT",FACE,{"disambiguationData":[TD([[makeQuery(id+"F6.imprint","IMPRINT",EDGE,{"derivedFrom":sQuery(id+"F6.wireOp",EDGE,"E8.1.4.0")}),1.0]])]});
            var Q5;
            Q5=makeQuery(id+"F6.imprint","IMPRINT",FACE,{"disambiguationData":[TD([[makeQuery(id+"F6.imprint","IMPRINT",EDGE,{"derivedFrom":sQuery(id+"F6.wireOp",EDGE,"E8.1.5.0")}),1.0]])]});
            var Q6;
            Q6=makeQuery(id+"F6.imprint","IMPRINT",FACE,{"disambiguationData":[TD([[makeQuery(id+"F6.imprint","IMPRINT",EDGE,{"derivedFrom":sQuery(id+"F6.wireOp",EDGE,"E8.1.6.0")}),1.0]])]});
            var Q7;
            Q7=makeQuery(id+"F6.imprint","IMPRINT",FACE,{"disambiguationData":[TD([[makeQuery(id+"F6.imprint","IMPRINT",EDGE,{"derivedFrom":sQuery(id+"F6.wireOp",EDGE,"E8.1.7.0")}),1.0]])]});
            var Q8;
            Q8=makeQuery(id+"F6.imprint","IMPRINT",FACE,{"disambiguationData":[TD([[makeQuery(id+"F6.imprint","IMPRINT",EDGE,{"derivedFrom":sQuery(id+"F6.wireOp",EDGE,"E8.2.0.0")}),1.0]])]});
            var Q9;
            Q9=makeQuery(id+"F6.imprint","IMPRINT",FACE,{"disambiguationData":[TD([[makeQuery(id+"F6.imprint","IMPRINT",EDGE,{"derivedFrom":sQuery(id+"F6.wireOp",EDGE,"E8.2.1.0")}),1.0]])]});
            var Q10;
            Q10=makeQuery(id+"F6.imprint","IMPRINT",FACE,{"disambiguationData":[TD([[makeQuery(id+"F6.imprint","IMPRINT",EDGE,{"derivedFrom":sQuery(id+"F6.wireOp",EDGE,"E8.2.2.0")}),1.0]])]});
            var Q11;
            Q11=makeQuery(id+"F6.imprint","IMPRINT",FACE,{"disambiguationData":[TD([[makeQuery(id+"F6.imprint","IMPRINT",EDGE,{"derivedFrom":sQuery(id+"F6.wireOp",EDGE,"E8.5.3.0")}),1.0]])]});
            var Q12;
            Q12=makeQuery(id+"F6.imprint","IMPRINT",FACE,{"disambiguationData":[TD([[makeQuery(id+"F6.imprint","IMPRINT",EDGE,{"derivedFrom":sQuery(id+"F6.wireOp",EDGE,"E8.5.4.0")}),1.0]])]});
            var Q13;
            Q13=makeQuery(id+"F6.imprint","IMPRINT",FACE,{"disambiguationData":[TD([[makeQuery(id+"F6.imprint","IMPRINT",EDGE,{"derivedFrom":sQuery(id+"F6.wireOp",EDGE,"E8.5.5.0")}),1.0]])]});
            var Q14;
            Q14=makeQuery(id+"F6.imprint","IMPRINT",FACE,{"disambiguationData":[TD([[makeQuery(id+"F6.imprint","IMPRINT",EDGE,{"derivedFrom":sQuery(id+"F6.wireOp",EDGE,"E8.5.6.0")}),1.0]])]});
            var Q15;
            Q15=makeQuery(id+"F6.imprint","IMPRINT",FACE,{"disambiguationData":[TD([[makeQuery(id+"F6.imprint","IMPRINT",EDGE,{"derivedFrom":sQuery(id+"F6.wireOp",EDGE,"E8.5.7.0")}),1.0]])]});
            var Q16;
            Q16=makeQuery(id+"F6.imprint","IMPRINT",FACE,{"disambiguationData":[TD([[makeQuery(id+"F6.imprint","IMPRINT",EDGE,{"derivedFrom":sQuery(id+"F6.wireOp",EDGE,"E8.6.0.0")}),1.0]])]});
            var Q17;
            Q17=makeQuery(id+"F6.imprint","IMPRINT",FACE,{"disambiguationData":[TD([[makeQuery(id+"F6.imprint","IMPRINT",EDGE,{"derivedFrom":sQuery(id+"F6.wireOp",EDGE,"E8.6.1.0")}),1.0]])]});
            var Q18;
            Q18=makeQuery(id+"F6.imprint","IMPRINT",FACE,{"disambiguationData":[TD([[makeQuery(id+"F6.imprint","IMPRINT",EDGE,{"derivedFrom":sQuery(id+"F6.wireOp",EDGE,"E8.6.2.0")}),1.0]])]});
            var Q19;
            Q19=makeQuery(id+"F6.imprint","IMPRINT",FACE,{"disambiguationData":[TD([[makeQuery(id+"F6.imprint","IMPRINT",EDGE,{"derivedFrom":sQuery(id+"F6.wireOp",EDGE,"E8.6.3.0")}),1.0]])]});
            var Q20;
            Q20=makeQuery(id+"F6.imprint","IMPRINT",FACE,{"disambiguationData":[TD([[makeQuery(id+"F6.imprint","IMPRINT",EDGE,{"derivedFrom":sQuery(id+"F6.wireOp",EDGE,"E8.6.4.0")}),1.0]])]});
            var Q21;
            Q21=makeQuery(id+"F6.imprint","IMPRINT",FACE,{"disambiguationData":[TD([[makeQuery(id+"F6.imprint","IMPRINT",EDGE,{"derivedFrom":sQuery(id+"F6.wireOp",EDGE,"E8.6.5.0")}),1.0]])]});
            var Q22;
            Q22=makeQuery(id+"F6.imprint","IMPRINT",FACE,{"disambiguationData":[TD([[makeQuery(id+"F6.imprint","IMPRINT",EDGE,{"derivedFrom":sQuery(id+"F6.wireOp",EDGE,"E8.6.6.0")}),1.0]])]});
            var Q23;
            Q23=makeQuery(id+"F6.imprint","IMPRINT",FACE,{"disambiguationData":[TD([[makeQuery(id+"F6.imprint","IMPRINT",EDGE,{"derivedFrom":sQuery(id+"F6.wireOp",EDGE,"E8.6.7.0")}),1.0]])]});
            var Q24;
            Q24=makeQuery(id+"F6.imprint","IMPRINT",FACE,{"disambiguationData":[TD([[makeQuery(id+"F6.imprint","IMPRINT",EDGE,{"derivedFrom":sQuery(id+"F6.wireOp",EDGE,"E8.5.2.0")}),1.0]])]});
            var Q25;
            Q25=makeQuery(id+"F6.imprint","IMPRINT",FACE,{"disambiguationData":[TD([[makeQuery(id+"F6.imprint","IMPRINT",EDGE,{"derivedFrom":sQuery(id+"F6.wireOp",EDGE,"E8.5.1.0")}),1.0]])]});
            var Q26;
            Q26=makeQuery(id+"F6.imprint","IMPRINT",FACE,{"disambiguationData":[TD([[makeQuery(id+"F6.imprint","IMPRINT",EDGE,{"derivedFrom":sQuery(id+"F6.wireOp",EDGE,"E8.5.0.0")}),1.0]])]});
            var Q27;
            Q27=makeQuery(id+"F6.imprint","IMPRINT",FACE,{"disambiguationData":[TD([[makeQuery(id+"F6.imprint","IMPRINT",EDGE,{"derivedFrom":sQuery(id+"F6.wireOp",EDGE,"E8.4.7.0")}),1.0]])]});
            var Q28;
            Q28=makeQuery(id+"F6.imprint","IMPRINT",FACE,{"disambiguationData":[TD([[makeQuery(id+"F6.imprint","IMPRINT",EDGE,{"derivedFrom":sQuery(id+"F6.wireOp",EDGE,"E8.4.6.0")}),1.0]])]});
            var Q29;
            Q29=makeQuery(id+"F6.imprint","IMPRINT",FACE,{"disambiguationData":[TD([[makeQuery(id+"F6.imprint","IMPRINT",EDGE,{"derivedFrom":sQuery(id+"F6.wireOp",EDGE,"E8.4.5.0")}),1.0]])]});
            var Q30;
            Q30=makeQuery(id+"F6.imprint","IMPRINT",FACE,{"disambiguationData":[TD([[makeQuery(id+"F6.imprint","IMPRINT",EDGE,{"derivedFrom":sQuery(id+"F6.wireOp",EDGE,"E8.4.4.0")}),1.0]])]});
            var Q31;
            Q31=makeQuery(id+"F6.imprint","IMPRINT",FACE,{"disambiguationData":[TD([[makeQuery(id+"F6.imprint","IMPRINT",EDGE,{"derivedFrom":sQuery(id+"F6.wireOp",EDGE,"E8.4.3.0")}),1.0]])]});
            var Q32;
            Q32=makeQuery(id+"F6.imprint","IMPRINT",FACE,{"disambiguationData":[TD([[makeQuery(id+"F6.imprint","IMPRINT",EDGE,{"derivedFrom":sQuery(id+"F6.wireOp",EDGE,"E8.4.2.0")}),1.0]])]});
            var Q33;
            Q33=makeQuery(id+"F6.imprint","IMPRINT",FACE,{"disambiguationData":[TD([[makeQuery(id+"F6.imprint","IMPRINT",EDGE,{"derivedFrom":sQuery(id+"F6.wireOp",EDGE,"E8.4.1.0")}),1.0]])]});
            var Q34;
            Q34=makeQuery(id+"F6.imprint","IMPRINT",FACE,{"disambiguationData":[TD([[makeQuery(id+"F6.imprint","IMPRINT",EDGE,{"derivedFrom":sQuery(id+"F6.wireOp",EDGE,"E8.4.0.0")}),1.0]])]});
            var Q35;
            Q35=makeQuery(id+"F6.imprint","IMPRINT",FACE,{"disambiguationData":[TD([[makeQuery(id+"F6.imprint","IMPRINT",EDGE,{"derivedFrom":sQuery(id+"F6.wireOp",EDGE,"E8.3.7.0")}),1.0]])]});
            var Q36;
            Q36=makeQuery(id+"F6.imprint","IMPRINT",FACE,{"disambiguationData":[TD([[makeQuery(id+"F6.imprint","IMPRINT",EDGE,{"derivedFrom":sQuery(id+"F6.wireOp",EDGE,"E8.3.6.0")}),1.0]])]});
            var Q37;
            Q37=makeQuery(id+"F6.imprint","IMPRINT",FACE,{"disambiguationData":[TD([[makeQuery(id+"F6.imprint","IMPRINT",EDGE,{"derivedFrom":sQuery(id+"F6.wireOp",EDGE,"E8.3.5.0")}),1.0]])]});
            var Q38;
            Q38=makeQuery(id+"F6.imprint","IMPRINT",FACE,{"disambiguationData":[TD([[makeQuery(id+"F6.imprint","IMPRINT",EDGE,{"derivedFrom":sQuery(id+"F6.wireOp",EDGE,"E8.3.4.0")}),1.0]])]});
            var Q39;
            Q39=makeQuery(id+"F6.imprint","IMPRINT",FACE,{"disambiguationData":[TD([[makeQuery(id+"F6.imprint","IMPRINT",EDGE,{"derivedFrom":sQuery(id+"F6.wireOp",EDGE,"E8.3.3.0")}),1.0]])]});
            var Q40;
            Q40=makeQuery(id+"F6.imprint","IMPRINT",FACE,{"disambiguationData":[TD([[makeQuery(id+"F6.imprint","IMPRINT",EDGE,{"derivedFrom":sQuery(id+"F6.wireOp",EDGE,"E8.3.2.0")}),1.0]])]});
            var Q41;
            Q41=makeQuery(id+"F6.imprint","IMPRINT",FACE,{"disambiguationData":[TD([[makeQuery(id+"F6.imprint","IMPRINT",EDGE,{"derivedFrom":sQuery(id+"F6.wireOp",EDGE,"E8.3.1.0")}),1.0]])]});
            var Q42;
            Q42=makeQuery(id+"F6.imprint","IMPRINT",FACE,{"disambiguationData":[TD([[makeQuery(id+"F6.imprint","IMPRINT",EDGE,{"derivedFrom":sQuery(id+"F6.wireOp",EDGE,"E8.3.0.0")}),1.0]])]});
            var Q43;
            Q43=makeQuery(id+"F6.imprint","IMPRINT",FACE,{"disambiguationData":[TD([[makeQuery(id+"F6.imprint","IMPRINT",EDGE,{"derivedFrom":sQuery(id+"F6.wireOp",EDGE,"E8.2.7.0")}),1.0]])]});
            var Q44;
            Q44=makeQuery(id+"F6.imprint","IMPRINT",FACE,{"disambiguationData":[TD([[makeQuery(id+"F6.imprint","IMPRINT",EDGE,{"derivedFrom":sQuery(id+"F6.wireOp",EDGE,"E8.2.6.0")}),1.0]])]});
            var Q45;
            Q45=makeQuery(id+"F6.imprint","IMPRINT",FACE,{"disambiguationData":[TD([[makeQuery(id+"F6.imprint","IMPRINT",EDGE,{"derivedFrom":sQuery(id+"F6.wireOp",EDGE,"E8.2.5.0")}),1.0]])]});
            var Q46;
            Q46=makeQuery(id+"F6.imprint","IMPRINT",FACE,{"disambiguationData":[TD([[makeQuery(id+"F6.imprint","IMPRINT",EDGE,{"derivedFrom":sQuery(id+"F6.wireOp",EDGE,"E8.2.4.0")}),1.0]])]});
            var Q47;
            Q47=makeQuery(id+"F6.imprint","IMPRINT",FACE,{"disambiguationData":[TD([[makeQuery(id+"F6.imprint","IMPRINT",EDGE,{"derivedFrom":sQuery(id+"F6.wireOp",EDGE,"E8.2.3.0")}),1.0]])]});
            var Q48;
            Q48=makeQuery(id+"F6.imprint","IMPRINT",FACE,{"disambiguationData":[TD([[makeQuery(id+"F6.imprint","IMPRINT",EDGE,{"derivedFrom":sQuery(id+"F6.wireOp",EDGE,"E8.0.7.0")}),1.0]])]});
            var Q49;
            Q49=makeQuery(id+"F6.imprint","IMPRINT",FACE,{"disambiguationData":[TD([[makeQuery(id+"F6.imprint","IMPRINT",EDGE,{"derivedFrom":sQuery(id+"F6.wireOp",EDGE,"E8.0.6.0")}),1.0]])]});
            var Q50;
            Q50=makeQuery(id+"F6.imprint","IMPRINT",FACE,{"disambiguationData":[TD([[makeQuery(id+"F6.imprint","IMPRINT",EDGE,{"derivedFrom":sQuery(id+"F6.wireOp",EDGE,"E8.0.5.0")}),1.0]])]});
            var Q51;
            Q51=makeQuery(id+"F6.imprint","IMPRINT",FACE,{"disambiguationData":[TD([[makeQuery(id+"F6.imprint","IMPRINT",EDGE,{"derivedFrom":sQuery(id+"F6.wireOp",EDGE,"E8.0.4.0")}),1.0]])]});
            var Q52;
            Q52=makeQuery(id+"F6.imprint","IMPRINT",FACE,{"disambiguationData":[TD([[makeQuery(id+"F6.imprint","IMPRINT",EDGE,{"derivedFrom":sQuery(id+"F6.wireOp",EDGE,"E8.0.3.0")}),1.0]])]});
            var Q53;
            Q53=makeQuery(id+"F6.imprint","IMPRINT",FACE,{"disambiguationData":[TD([[makeQuery(id+"F6.imprint","IMPRINT",EDGE,{"derivedFrom":sQuery(id+"F6.wireOp",EDGE,"E8.0.2.0")}),1.0]])]});
            var Q54;
            Q54=makeQuery(id+"F6.imprint","IMPRINT",FACE,{"disambiguationData":[TD([[makeQuery(id+"F6.imprint","IMPRINT",EDGE,{"derivedFrom":sQuery(id+"F6.wireOp",EDGE,"E8.0.1.0")}),1.0]])]});
            var Q55;
            Q55=makeQuery(id+"F6.imprint","IMPRINT",FACE,{"disambiguationData":[TD([[makeQuery(id+"F6.imprint","IMPRINT",EDGE,{"derivedFrom":sQuery(id+"F6.wireOp",EDGE,"E7.bottom")}),1.0]])]});
            var Q56;
            Q56=makeQuery(id+"F6.imprint","IMPRINT",FACE,{"disambiguationData":[TD([[makeQuery(id+"F6.imprint","IMPRINT",EDGE,{"derivedFrom":sQuery(id+"F6.wireOp",EDGE,"E8.7.0.0")}),1.0]])]});
            var Q57;
            Q57=makeQuery(id+"F6.imprint","IMPRINT",FACE,{"disambiguationData":[TD([[makeQuery(id+"F6.imprint","IMPRINT",EDGE,{"derivedFrom":sQuery(id+"F6.wireOp",EDGE,"E8.7.1.0")}),1.0]])]});
            var Q58;
            Q58=makeQuery(id+"F6.imprint","IMPRINT",FACE,{"disambiguationData":[TD([[makeQuery(id+"F6.imprint","IMPRINT",EDGE,{"derivedFrom":sQuery(id+"F6.wireOp",EDGE,"E8.7.2.0")}),1.0]])]});
            var Q59;
            Q59=makeQuery(id+"F6.imprint","IMPRINT",FACE,{"disambiguationData":[TD([[makeQuery(id+"F6.imprint","IMPRINT",EDGE,{"derivedFrom":sQuery(id+"F6.wireOp",EDGE,"E8.7.3.0")}),1.0]])]});
            var Q60;
            Q60=makeQuery(id+"F6.imprint","IMPRINT",FACE,{"disambiguationData":[TD([[makeQuery(id+"F6.imprint","IMPRINT",EDGE,{"derivedFrom":sQuery(id+"F6.wireOp",EDGE,"E8.7.4.0")}),1.0]])]});
            var Q61;
            Q61=makeQuery(id+"F6.imprint","IMPRINT",FACE,{"disambiguationData":[TD([[makeQuery(id+"F6.imprint","IMPRINT",EDGE,{"derivedFrom":sQuery(id+"F6.wireOp",EDGE,"E8.7.5.0")}),1.0]])]});
            var Q62;
            Q62=makeQuery(id+"F6.imprint","IMPRINT",FACE,{"disambiguationData":[TD([[makeQuery(id+"F6.imprint","IMPRINT",EDGE,{"derivedFrom":sQuery(id+"F6.wireOp",EDGE,"E8.7.6.0")}),1.0]])]});
            var Q63;
            Q63=makeQuery(id+"F6.imprint","IMPRINT",FACE,{"disambiguationData":[TD([[makeQuery(id+"F6.imprint","IMPRINT",EDGE,{"derivedFrom":sQuery(id+"F6.wireOp",EDGE,"E8.7.7.0")}),1.0]])]});
            extrude(context, id + "F7", {"entities" : qUnion([Q0, Q1, Q2, Q3, Q4, Q5, Q6, Q7, Q8, Q9, Q10, Q11, Q12, Q13, Q14, Q15, Q16, Q17, Q18, Q19, Q20, Q21, Q22, Q23, Q24, Q25, Q26, Q27, Q28, Q29, Q30, Q31, Q32, Q33, Q34, Q35, Q36, Q37, Q38, Q39, Q40, Q41, Q42, Q43, Q44, Q45, Q46, Q47, Q48, Q49, Q50, Q51, Q52, Q53, Q54, Q55, Q56, Q57, Q58, Q59, Q60, Q61, Q62, Q63]), "operationType" : NewBodyOperationType.REMOVE, "oppositeDirection" : true, "depth" : 30 * mm, "offsetDistance" : 25 * mm});
        }
    });
